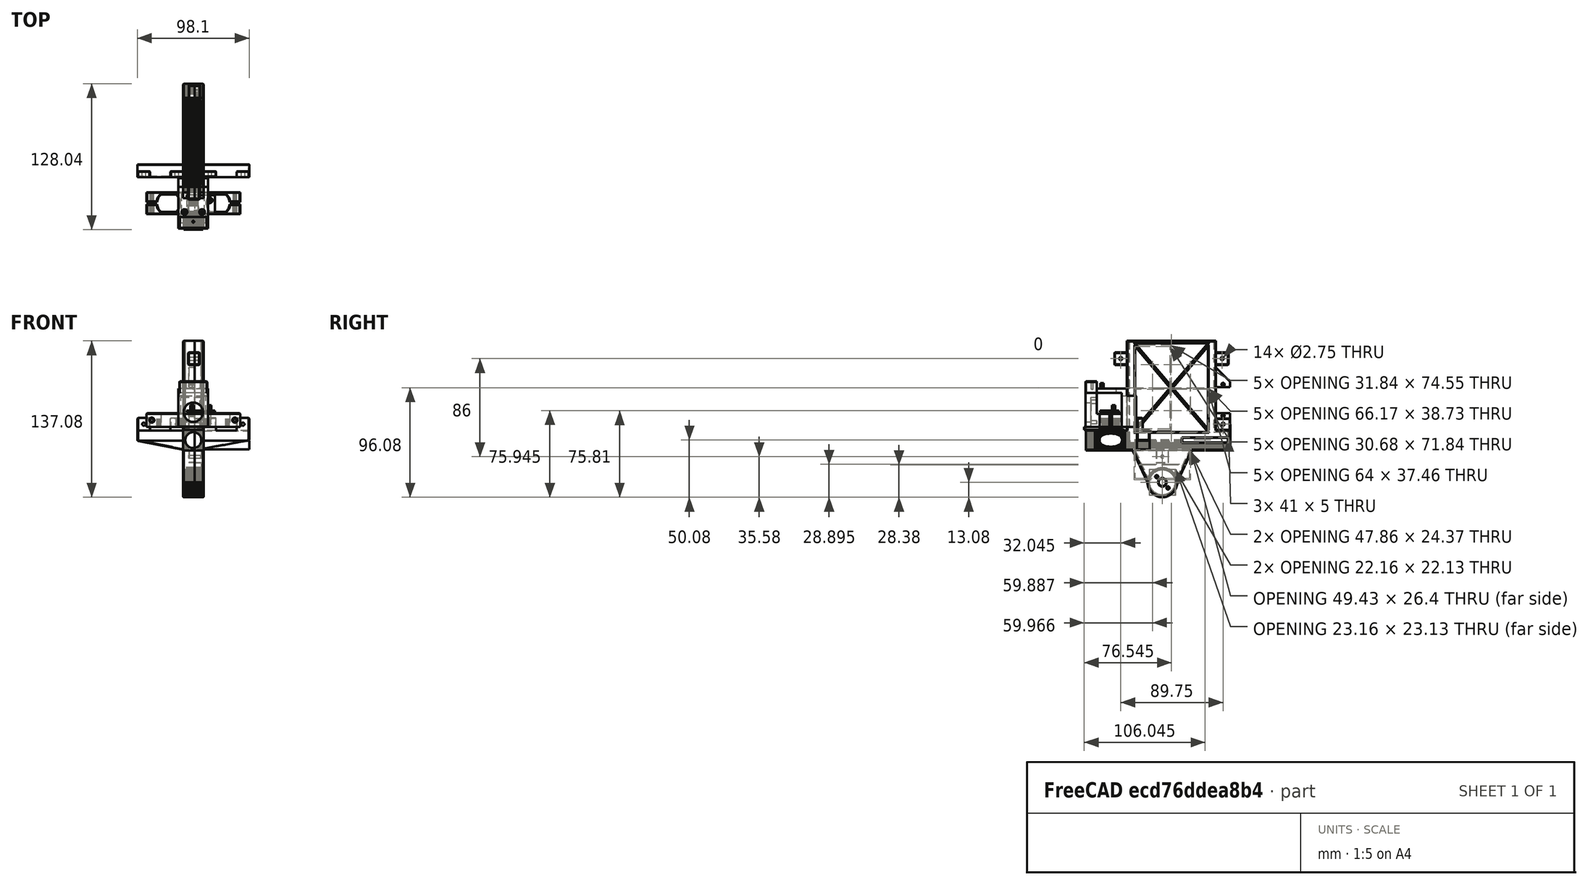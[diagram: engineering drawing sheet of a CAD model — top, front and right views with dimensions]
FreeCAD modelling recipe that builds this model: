
FCSTD DOCUMENT  (FreeCAD 1.0R39109 (Git))
Label: turret
License: All rights reserved
LicenseURL: https://en.wikipedia.org/wiki/All_rights_reserved
objects: Sketcher::SketchObject×55, Part::Extrusion×53, Part::Cut×36, Part::MultiFuse×25, Part::Feature×16, Part::Chamfer×14, Part::Box×11, Part::Fuse×8, Mesh::Feature×7, Part::Refine×4
note: 277 computed .brp shape members not serialized (recipe doc carries the construction recipe); baked Part::Feature solids carry a one-line shape summary decoded from their .brp

FEATURE [Part::Box] Box  label="querbalken"
  AttacherType = Attacher::AttachEngine3D
  Height = 30
  Length = 100
  Placement = pos=(43.7,-64,0) rot=(0,0,1;0rad)
  Width = 45
FEATURE [Part::Feature] MPU_6050_GY_521_mount002_solid  label="gyro"
  Placement = pos=(81.27,-54.1,29) rot=(0,0,1;3.14159rad)
  shape: bbox 24.5 x 16.43 x 6 mm, 2020 faces (baked)
FEATURE [Part::Box] Box001  label="basis"
  AttacherType = Attacher::AttachEngine3D
  Height = 26
  Length = 22
  Placement = pos=(38,80,2) rot=(0,0,1;0rad)
  Width = 34
FEATURE [Sketcher::SketchObject] Sketch002  label="sketch_aufnahmen"
  ArcFitTolerance = 1e-06
  AttachmentSupport = -> [Box001]
  ExternalGeometry = -> [Box001]
  FullyConstrained = true
  MakeInternals = false
  MapMode = 5
  Placement = pos=(38,80,2) rot=(1,0,0;1.5708rad)
  sketch-geometry (2):
    g0: Circle CenterX=18 CenterY=22 CenterZ=0 NormalX=0 NormalY=0 NormalZ=1 AngleXU=0 Radius=1.45
    g1: Circle CenterX=4 CenterY=4 CenterZ=0 NormalX=0 NormalY=0 NormalZ=1 AngleXU=0 Radius=1.45
  constraints (6):
    c: Diameter(g0) = 2.9
    c: Distance(g0,g-3) = 4
    c: Distance(g0,g-4) = 4
    c: Diameter(g1) = 2.9
    c: DistanceY(g-1,g1) = 4
    c: DistanceX(g-2,g1) = 4
FEATURE [Part::Extrusion] Extrude  label="extrude_aufnahmen"
  Base = -> Sketch002
  Dir = (0,-1,2e-16)
  DirMode = 2
  FaceMakerClass = Part::FaceMakerBullseye
  FaceMakerMode = 3
  LengthFwd = -5
  LengthRev = 0
  Solid = true
  Symmetric = false
FEATURE [Part::Cut] Cut
  Base = -> Box001
  Placement = pos=(0,-69,0) rot=(0,0,1;0rad)
  Refine = true
  Tool = -> Extrude
FEATURE [Sketcher::SketchObject] Sketch  label="sketch_sensor"
  ArcFitTolerance = 1e-06
  AttachmentSupport = -> [Cut]
  ExternalGeometry = -> [Cut]
  FullyConstrained = true
  MakeInternals = false
  MapMode = 5
  Placement = pos=(0,11,0) rot=(1,0,0;1.5708rad)
  sketch-geometry (1):
    g0: Circle CenterX=49 CenterY=15 CenterZ=0 NormalX=0 NormalY=0 NormalZ=1 AngleXU=0 Radius=8.5
  constraints (3):
    c: Diameter(g0) = 17
    c: Distance(g0,g-3) = 13
    c: Distance(g0,g-4) = 11
FEATURE [Part::Extrusion] Extrude001  label="extrude_sensor"
  Base = -> Sketch
  Dir = (0,-1,2e-16)
  DirMode = 2
  FaceMakerClass = Part::FaceMakerBullseye
  FaceMakerMode = 3
  LengthFwd = 20
  LengthRev = 0
  Solid = true
  Symmetric = false
FEATURE [Part::Fuse] Fusion  label="ultraschall"
  Base = -> Cut
  Placement = pos=(44.6,-2.9,0) rot=(0,0,1;0rad)
  Refine = true
  Tool = -> Extrude001
FEATURE [Part::Feature] Left_Magazine001
  shape: bbox 8 x 119 x 137.1 mm, 2276 faces, 0 solids (baked)
FEATURE [Part::Feature] Right_Magazine001
  shape: bbox 10 x 119 x 137.1 mm, 2082 faces, 0 solids (baked)
FEATURE [Part::Refine] Left_Magazine002
  Source = -> Left_Magazine001
FEATURE [Part::Refine] Right_Magazine002
  Source = -> Right_Magazine001
FEATURE [Part::Feature] Left_Magazine002_solid  label="mag_l"
  shape: bbox 8 x 119 x 137.1 mm, 1376 faces (baked)
FEATURE [Part::Feature] Right_Magazine002_solid  label="mag_r"
  shape: bbox 10 x 119 x 137.1 mm, 1299 faces (baked)
FEATURE [Part::MultiFuse] Fusion001  label="mag"
  Refine = true
  Shapes = -> [Left_Magazine002_solid,Right_Magazine002_solid]
FEATURE [Sketcher::SketchObject] Sketch004  label="muzzle_extension"
  ArcFitTolerance = 1e-06
  AttachmentSupport = -> [Fusion001]
  ExternalGeometry = -> [Fusion001]
  FullyConstrained = true
  MakeInternals = false
  MapMode = 5
  Placement = pos=(0,-53.6552,0) rot=(1,0,0;1.5708rad)
  sketch-geometry (63):
    g0: LineSegment StartX=-27.5 StartY=169.88 StartZ=0 EndX=-10.5 EndY=169.88 EndZ=0
    g1: LineSegment StartX=-10.5 StartY=169.88 StartZ=0 EndX=-10.5 EndY=151.88 EndZ=0
    g2: LineSegment StartX=-10.5 StartY=151.88 StartZ=0 EndX=-27.5 EndY=151.88 EndZ=0
    g3: LineSegment StartX=-27.5 StartY=151.88 StartZ=0 EndX=-27.5 EndY=169.88 EndZ=0
    g4: LineSegment StartX=-22.9905 StartY=166.631 StartZ=0 EndX=-22.3526 EndY=167.025 EndZ=0
    g5: LineSegment StartX=-22.3526 StartY=167.025 StartZ=0 EndX=-21.6763 EndY=167.348 EndZ=0
    g6: LineSegment StartX=-21.6763 StartY=167.348 StartZ=0 EndX=-20.9694 EndY=167.597 EndZ=0
    g7: LineSegment StartX=-20.9694 StartY=167.597 StartZ=0 EndX=-20.2398 EndY=167.77 EndZ=0
    g8: LineSegment StartX=-20.2398 StartY=167.77 StartZ=0 EndX=-19.496 EndY=167.863 EndZ=0
    g9: LineSegment StartX=-19.496 StartY=167.863 StartZ=0 EndX=-18.7466 EndY=167.876 EndZ=0
    g10: LineSegment StartX=-18.7466 StartY=167.876 StartZ=0 EndX=-18 EndY=167.808 EndZ=0
    g11: LineSegment StartX=-18 StartY=167.808 StartZ=0 EndX=-17.2744 EndY=167.664 EndZ=0
    g12: LineSegment StartX=-17.2744 StartY=167.664 StartZ=0 EndX=-16.568 EndY=167.444 EndZ=0
    g13: LineSegment StartX=-16.568 StartY=167.444 StartZ=0 EndX=-15.8889 EndY=167.151 EndZ=0
    g14: LineSegment StartX=-15.8889 StartY=167.151 StartZ=0 EndX=-15.2444 EndY=166.787 EndZ=0
    g15: LineSegment StartX=-15.2444 StartY=166.787 StartZ=0 EndX=-14.642 EndY=166.358 EndZ=0
    g16: LineSegment StartX=-14.642 StartY=166.358 StartZ=0 EndX=-14.0882 EndY=165.868 EndZ=0
    g17: LineSegment StartX=-14.0882 StartY=165.868 StartZ=0 EndX=-13.5892 EndY=165.321 EndZ=0
    g18: LineSegment StartX=-13.5892 StartY=165.321 StartZ=0 EndX=-13.1507 EndY=164.725 EndZ=0
    g19: LineSegment StartX=-13.1507 StartY=164.725 StartZ=0 EndX=-12.7776 EndY=164.087 EndZ=0
    g20: LineSegment StartX=-12.7776 StartY=164.087 StartZ=0 EndX=-12.4739 EndY=163.412 EndZ=0
    g21: LineSegment StartX=-12.4739 StartY=163.412 StartZ=0 EndX=-12.2431 EndY=162.709 EndZ=0
    g22: LineSegment StartX=-12.2431 StartY=162.709 StartZ=0 EndX=-12.0879 EndY=161.986 EndZ=0
    g23: LineSegment StartX=-12.0879 StartY=161.986 StartZ=0 EndX=-12.0098 EndY=161.25 EndZ=0
    g24: LineSegment StartX=-12.0098 StartY=161.25 StartZ=0 EndX=-12.0098 EndY=160.51 EndZ=0
    g25: LineSegment StartX=-12.0098 StartY=160.51 StartZ=0 EndX=-12.0879 EndY=159.775 EndZ=0
    g26: LineSegment StartX=-12.0879 StartY=159.775 StartZ=0 EndX=-12.2431 EndY=159.051 EndZ=0
    g27: LineSegment StartX=-12.2431 StartY=159.051 StartZ=0 EndX=-12.4739 EndY=158.348 EndZ=0
    g28: LineSegment StartX=-12.4739 StartY=158.348 StartZ=0 EndX=-12.7776 EndY=157.674 EndZ=0
    g29: LineSegment StartX=-12.7776 StartY=157.674 StartZ=0 EndX=-13.1507 EndY=157.035 EndZ=0
    g30: LineSegment StartX=-13.1507 StartY=157.035 StartZ=0 EndX=-13.5892 EndY=156.439 EndZ=0
    g31: LineSegment StartX=-13.5892 StartY=156.439 StartZ=0 EndX=-14.0882 EndY=155.893 EndZ=0
    g32: LineSegment StartX=-14.0882 StartY=155.893 StartZ=0 EndX=-14.642 EndY=155.402 EndZ=0
    g33: LineSegment StartX=-14.642 StartY=155.402 StartZ=0 EndX=-15.2444 EndY=154.973 EndZ=0
    g34: LineSegment StartX=-15.2444 StartY=154.973 StartZ=0 EndX=-15.8889 EndY=154.61 EndZ=0
    g35: LineSegment StartX=-15.8889 StartY=154.61 StartZ=0 EndX=-16.568 EndY=154.316 EndZ=0
    g36: LineSegment StartX=-16.568 StartY=154.316 StartZ=0 EndX=-17.2744 EndY=154.096 EndZ=0
    g37: LineSegment StartX=-17.2744 StartY=154.096 StartZ=0 EndX=-18 EndY=153.952 EndZ=0
    g38: LineSegment StartX=-18 StartY=153.952 StartZ=0 EndX=-18.7466 EndY=153.885 EndZ=0
    g39: LineSegment StartX=-18.7466 StartY=153.885 StartZ=0 EndX=-19.496 EndY=153.898 EndZ=0
    g40: LineSegment StartX=-19.496 StartY=153.898 StartZ=0 EndX=-20.2398 EndY=153.991 EndZ=0
    g41: LineSegment StartX=-20.2398 StartY=153.991 StartZ=0 EndX=-20.9694 EndY=154.163 EndZ=0
    g42: LineSegment StartX=-20.9694 StartY=154.163 StartZ=0 EndX=-21.6763 EndY=154.412 EndZ=0
    g43: LineSegment StartX=-21.6763 StartY=154.412 StartZ=0 EndX=-22.3526 EndY=154.735 EndZ=0
    g44: LineSegment StartX=-22.3526 StartY=154.735 StartZ=0 EndX=-22.9905 EndY=155.129 EndZ=0
    g45: LineSegment StartX=-22.9905 StartY=155.129 StartZ=0 EndX=-23.5826 EndY=155.589 EndZ=0
    g46: LineSegment StartX=-23.5826 StartY=155.589 StartZ=0 EndX=-24.1221 EndY=156.109 EndZ=0
    g47: LineSegment StartX=-24.1221 StartY=156.109 StartZ=0 EndX=-24.6029 EndY=156.684 EndZ=0
    g48: LineSegment StartX=-24.6029 StartY=156.684 StartZ=0 EndX=-25.0195 EndY=157.307 EndZ=0
    g49: LineSegment StartX=-25.0195 StartY=157.307 StartZ=0 EndX=-25.367 EndY=157.971 EndZ=0
    g50: LineSegment StartX=-25.367 StartY=157.971 StartZ=0 EndX=-25.6416 EndY=158.669 EndZ=0
    g51: LineSegment StartX=-25.6416 StartY=158.669 StartZ=0 EndX=-25.8399 EndY=159.392 EndZ=0
    g52: LineSegment StartX=-25.8399 StartY=159.392 StartZ=0 EndX=-25.9599 EndY=160.132 EndZ=0
    g53: LineSegment StartX=-25.9599 StartY=160.132 StartZ=0 EndX=-26 EndY=160.88 EndZ=0
    g54: LineSegment StartX=-26 StartY=160.88 StartZ=0 EndX=-25.9599 EndY=161.629 EndZ=0
    g55: LineSegment StartX=-25.9599 StartY=161.629 StartZ=0 EndX=-25.8399 EndY=162.369 EndZ=0
    g56: LineSegment StartX=-25.8399 StartY=162.369 StartZ=0 EndX=-25.6416 EndY=163.091 EndZ=0
    g57: LineSegment StartX=-25.6416 StartY=163.091 StartZ=0 EndX=-25.367 EndY=163.789 EndZ=0
    g58: LineSegment StartX=-25.367 StartY=163.789 StartZ=0 EndX=-25.0195 EndY=164.453 EndZ=0
    g59: LineSegment StartX=-25.0195 StartY=164.453 StartZ=0 EndX=-24.6029 EndY=165.076 EndZ=0
    g60: LineSegment StartX=-24.6029 StartY=165.076 StartZ=0 EndX=-24.1221 EndY=165.651 EndZ=0
    g61: LineSegment StartX=-24.1221 StartY=165.651 StartZ=0 EndX=-23.5826 EndY=166.172 EndZ=0
    g62: LineSegment StartX=-23.5826 StartY=166.172 StartZ=0 EndX=-22.9905 EndY=166.631 EndZ=0
  constraints (126):
    c: Coincident(g-6,g0)
    c: Coincident(g0,g-6)
    c: Coincident(g0,g1)
    c: Coincident(g1,g-5)
    c: Coincident(g1,g2)
    c: Coincident(g2,g-4)
    c: Coincident(g2,g3)
    c: Coincident(g3,g0)
    c: Coincident(g-67,g4)
    c: Coincident(g4,g-67)
    c: Coincident(g4,g5)
    c: Coincident(g5,g-8)
    c: Coincident(g5,g6)
    c: Coincident(g6,g-8)
    c: Coincident(g6,g7)
    c: Coincident(g7,g-10)
    c: Coincident(g7,g8)
    c: Coincident(g8,g-11)
    c: Coincident(g8,g9)
    c: Coincident(g9,g-12)
    c: Coincident(g9,g10)
    c: Coincident(g10,g-13)
    c: Coincident(g10,g11)
    c: Coincident(g11,g-14)
    c: Coincident(g11,g12)
    c: Coincident(g12,g-15)
    c: Coincident(g12,g13)
    c: Coincident(g13,g-16)
    c: Coincident(g13,g14)
    c: Coincident(g14,g-17)
    c: Coincident(g14,g15)
    c: Coincident(g15,g-18)
    c: Coincident(g15,g16)
    c: Coincident(g16,g-19)
    c: Coincident(g16,g17)
    c: Coincident(g17,g-20)
    c: Coincident(g17,g18)
    c: Coincident(g18,g-21)
    c: Coincident(g18,g19)
    c: Coincident(g19,g-22)
    c: Coincident(g19,g20)
    c: Coincident(g20,g-24)
    c: Coincident(g20,g21)
    c: Coincident(g21,g-25)
    c: Coincident(g21,g22)
    c: Coincident(g22,g-26)
    c: Coincident(g22,g23)
    c: Coincident(g23,g-27)
    c: Coincident(g23,g24)
    c: Coincident(g24,g-28)
    c: Coincident(g24,g25)
    c: Coincident(g25,g-29)
    c: Coincident(g25,g26)
    c: Coincident(g26,g-30)
    c: Coincident(g26,g27)
    c: Coincident(g27,g-31)
    c: Coincident(g27,g28)
    c: Coincident(g28,g-32)
    c: Coincident(g28,g29)
    c: Coincident(g29,g-33)
    c: Coincident(g29,g30)
    c: Coincident(g30,g-34)
    c: Coincident(g30,g31)
    c: Coincident(g31,g-35)
    c: Coincident(g31,g32)
    c: Coincident(g32,g-36)
    c: Coincident(g32,g33)
    c: Coincident(g33,g-37)
    c: Coincident(g33,g34)
    c: Coincident(g34,g-38)
    c: Coincident(g34,g35)
    c: Coincident(g35,g-39)
    c: Coincident(g35,g36)
    c: Coincident(g36,g-41)
    c: Coincident(g36,g37)
    c: Coincident(g37,g-42)
    c: Coincident(g37,g38)
    c: Coincident(g38,g-43)
    c: Coincident(g38,g39)
    c: Coincident(g39,g-44)
    c: Coincident(g39,g40)
    c: Coincident(g40,g-45)
    c: Coincident(g40,g41)
    c: Coincident(g41,g-46)
    c: Coincident(g41,g42)
    c: Coincident(g42,g-47)
    c: Coincident(g42,g43)
    c: Coincident(g43,g-48)
    c: Coincident(g43,g44)
    c: Coincident(g44,g-49)
    c: Coincident(g44,g45)
    c: Coincident(g45,g-50)
    c: Coincident(g45,g46)
    c: Coincident(g46,g-51)
    c: Coincident(g46,g47)
    c: Coincident(g47,g-52)
    c: Coincident(g47,g48)
    c: Coincident(g48,g-53)
    c: Coincident(g48,g49)
    c: Coincident(g49,g-54)
    c: Coincident(g49,g50)
    c: Coincident(g50,g-55)
    c: Coincident(g50,g51)
    c: Coincident(g51,g-56)
    c: Coincident(g51,g52)
    c: Coincident(g52,g-57)
    c: Coincident(g52,g53)
    c: Coincident(g53,g-58)
    c: Coincident(g53,g54)
    c: Coincident(g54,g-59)
    c: Coincident(g54,g55)
    c: Coincident(g55,g-60)
    c: Coincident(g55,g56)
    c: Coincident(g56,g-61)
    c: Coincident(g56,g57)
    c: Coincident(g57,g-62)
    c: Coincident(g57,g58)
    c: Coincident(g58,g-63)
    c: Coincident(g58,g59)
    c: Coincident(g59,g-64)
    c: Coincident(g59,g60)
    c: Coincident(g60,g-65)
    c: Coincident(g60,g61)
    c: Coincident(g61,g-66)
    c: Coincident(g61,g62)
    c: Coincident(g62,g4)
FEATURE [Sketcher::SketchObject] Sketch007
  ArcFitTolerance = 1e-06
  AttachmentSupport = -> [Box]
  ExternalGeometry = -> [Box]
  FullyConstrained = true
  MakeInternals = false
  MapMode = 5
  Placement = pos=(43.7,-64,0) rot=(1,0,0;3.14159rad)
  sketch-geometry (17):
    g0: LineSegment [constr] StartX=0 StartY=-22.5 StartZ=0 EndX=100 EndY=-22.5 EndZ=0
    g1: LineSegment [constr] StartX=50 StartY=0 StartZ=0 EndX=50 EndY=-45 EndZ=0
    g2: LineSegment [constr] StartX=27.25 StartY=0 StartZ=0 EndX=27.25 EndY=-45 EndZ=0
    g3: LineSegment [constr] StartX=71.25 StartY=-20.5 StartZ=0 EndX=71.25 EndY=-24.5 EndZ=0
    g4: LineSegment [constr] StartX=71.25 StartY=-24.5 StartZ=0 EndX=74.25 EndY=-24.5 EndZ=0
    g5: LineSegment [constr] StartX=74.25 StartY=-24.5 StartZ=0 EndX=74.25 EndY=-20.5 EndZ=0
    g6: LineSegment [constr] StartX=74.25 StartY=-20.5 StartZ=0 EndX=71.25 EndY=-20.5 EndZ=0
    g7: LineSegment [constr] StartX=25.75 StartY=-20.5 StartZ=0 EndX=25.75 EndY=-24.5 EndZ=0
    g8: LineSegment [constr] StartX=25.75 StartY=-24.5 StartZ=0 EndX=28.75 EndY=-24.5 EndZ=0
    g9: LineSegment [constr] StartX=28.75 StartY=-24.5 StartZ=0 EndX=28.75 EndY=-20.5 EndZ=0
    g10: LineSegment [constr] StartX=28.75 StartY=-20.5 StartZ=0 EndX=25.75 EndY=-20.5 EndZ=0
    g11: LineSegment [constr] StartX=72.75 StartY=0 StartZ=0 EndX=72.75 EndY=-45 EndZ=0
    g12: LineSegment [constr] StartX=32.75 StartY=0 StartZ=0 EndX=32.75 EndY=-45 EndZ=0
    g13: LineSegment StartX=40.9 StartY=0 StartZ=0 EndX=40.9 EndY=-8.25 EndZ=0
    g14: LineSegment StartX=59.1 StartY=0 StartZ=0 EndX=59.1 EndY=-8.25 EndZ=0
    g15: LineSegment StartX=40.9 StartY=-8.25 StartZ=0 EndX=59.1 EndY=-8.25 EndZ=0
    g16: LineSegment StartX=40.9 StartY=0 StartZ=0 EndX=59.1 EndY=0 EndZ=0
  constraints (54):
    c: PointOnObject(g0,g-2)
    c: Symmetric(g-3,g-3,g0)
    c: Horizontal(g0)
    c: PointOnObject(g1,g-1)
    c: Symmetric(g-4,g-4,g1)
    c: Vertical(g1)
    c: PointOnObject(g2,g-1)
    c: PointOnObject(g2,g-4)
    c: Vertical(g2)
    c: Distance(g2,g1) = 22.75
    c: Coincident(g3,g4)
    c: Coincident(g4,g5)
    c: Coincident(g5,g6)
    c: Coincident(g6,g3)
    c: Vertical(g3)
    c: Vertical(g5)
    c: Horizontal(g4)
    c: Horizontal(g6)
    c: Distance(g5,g3) = 3
    c: Distance(g3,g4) = 5
    c: Coincident(g7,g8)
    c: Coincident(g8,g9)
    c: Coincident(g9,g10)
    c: Coincident(g10,g7)
    c: Vertical(g7)
    c: Vertical(g9)
    c: Horizontal(g8)
    c: Horizontal(g10)
    c: Distance(g9,g7) = 3
    c: Distance(g7,g8) = 5
    c: PointOnObject(g11,g-1)
    c: PointOnObject(g11,g-4)
    c: Vertical(g11)
    c: Distance(g11,g1) = 22.75
    c: Distance(g3,g11) = 1.5
    c: Distance(g4,g0) = 2
    c: Distance(g7,g2) = 1.5
    c: Distance(g8,g0) = 2
    c: PointOnObject(g12,g-1)
    c: PointOnObject(g12,g-4)
    c: Vertical(g12)
    c: Distance(g2,g12) = 5.5
    c: PointOnObject(g13,g-1)
    c: Vertical(g13)
    c: Distance(g13,g1) = 9.1
    c: PointOnObject(g14,g-1)
    c: Vertical(g14)
    c: Distance(g14,g1) = 9.1
    c: Coincident(g15,g13)
    c: Coincident(g15,g14)
    c: Horizontal(g15)
    c: Distance(g13,g0) = 14.25
    c: Coincident(g16,g13)
    c: Coincident(g16,g14)
FEATURE [Part::Feature] Fusion006  label="servo_cut_with_screw_r"
  shape: bbox 31 x 41.99 x 29 mm, 460 faces (baked)
FEATURE [Sketcher::SketchObject] Sketch011
  ArcFitTolerance = 1e-06
  AttachmentSupport = -> [Fusion006]
  ExternalGeometry = -> [Fusion006]
  FullyConstrained = true
  MakeInternals = false
  MapMode = 5
  Placement = pos=(45.95,0,0) rot=(0.57735,-0.57735,-0.57735;2.0944rad)
  sketch-geometry (4):
    g0: LineSegment StartX=34 StartY=3.5 StartZ=0 EndX=49 EndY=3.5 EndZ=0
    g1: LineSegment StartX=34 StartY=13.5 StartZ=0 EndX=49 EndY=13.5 EndZ=0
    g2: LineSegment StartX=34 StartY=13.5 StartZ=0 EndX=34 EndY=3.5 EndZ=0
    g3: LineSegment StartX=49 StartY=13.5 StartZ=0 EndX=49 EndY=3.5 EndZ=0
  constraints (12):
    c: PointOnObject(g0,g-3)
    c: PointOnObject(g0,g-4)
    c: Horizontal(g0)
    c: Distance(g0,g-3) = 3.5
    c: PointOnObject(g1,g-3)
    c: PointOnObject(g1,g-4)
    c: Horizontal(g1)
    c: DistanceY(g0,g1) = 10
    c: Coincident(g2,g1)
    c: Coincident(g2,g0)
    c: Coincident(g3,g1)
    c: Coincident(g3,g0)
FEATURE [Part::Extrusion] Extrude007
  Base = -> Sketch011
  Dir = (-1,0,0)
  DirMode = 2
  FaceMakerClass = Part::FaceMakerBullseye
  FaceMakerMode = 3
  LengthFwd = 10
  LengthRev = 0
  Solid = true
  Symmetric = false
FEATURE [Part::MultiFuse] Fusion007  label="servu_cut_with_screw_and_cabel_r"
  Refine = true
  Shapes = -> [Fusion006,Extrude007]
FEATURE [Sketcher::SketchObject] Sketch012
  ArcFitTolerance = 1e-06
  AttachmentSupport = -> [Fusion007]
  ExternalGeometry = -> [Fusion007]
  FullyConstrained = true
  MakeInternals = false
  MapMode = 5
  Placement = pos=(0,0,21.5) rot=(0,0,1;0rad)
  sketch-geometry (18):
    g0: LineSegment StartX=51.13 StartY=-34 StartZ=0 EndX=51.5875 EndY=-33.3211 EndZ=0
    g1: LineSegment StartX=51.5875 StartY=-33.3211 StartZ=0 EndX=52.0856 EndY=-32.6702 EndZ=0
    g2: LineSegment StartX=52.0856 StartY=-32.6702 StartZ=0 EndX=52.6209 EndY=-32.0496 EndZ=0
    g3: LineSegment StartX=52.6209 StartY=-32.0496 StartZ=0 EndX=53.1917 EndY=-31.4614 EndZ=0
    g4: LineSegment StartX=53.1917 StartY=-31.4614 StartZ=0 EndX=53.7958 EndY=-30.9075 EndZ=0
    g5: LineSegment StartX=53.7958 StartY=-30.9075 StartZ=0 EndX=54.4313 EndY=-30.39 EndZ=0
    g6: LineSegment StartX=54.4313 StartY=-30.39 StartZ=0 EndX=55.0961 EndY=-29.9106 EndZ=0
    g7: LineSegment StartX=55.0961 StartY=-29.9106 StartZ=0 EndX=45.95 EndY=-34 EndZ=0
    g8: LineSegment StartX=45.95 StartY=-34 StartZ=0 EndX=51.13 EndY=-34 EndZ=0
    g9: LineSegment StartX=45.95 StartY=-49 StartZ=0 EndX=51.1284 EndY=-49 EndZ=0
    g10: LineSegment StartX=51.1284 StartY=-49 StartZ=0 EndX=51.5875 EndY=-49.679 EndZ=0
    g11: LineSegment StartX=51.5875 StartY=-49.679 StartZ=0 EndX=52.0856 EndY=-50.3298 EndZ=0
    g12: LineSegment StartX=52.0856 StartY=-50.3298 StartZ=0 EndX=52.6209 EndY=-50.9505 EndZ=0
    g13: LineSegment StartX=52.6209 StartY=-50.9505 StartZ=0 EndX=53.1917 EndY=-51.5387 EndZ=0
    g14: LineSegment StartX=53.1917 StartY=-51.5387 StartZ=0 EndX=53.7958 EndY=-52.0925 EndZ=0
    g15: LineSegment StartX=53.7958 StartY=-52.0925 StartZ=0 EndX=54.4313 EndY=-52.6101 EndZ=0
    g16: LineSegment StartX=54.4313 StartY=-52.6101 StartZ=0 EndX=55.0961 EndY=-53.0895 EndZ=0
    g17: LineSegment StartX=55.0961 StartY=-53.0895 StartZ=0 EndX=45.95 EndY=-49 EndZ=0
  constraints (37):
    c: Coincident(g0,g-5)
    c: Coincident(g0,g1)
    c: Coincident(g1,g-6)
    c: Coincident(g1,g2)
    c: Coincident(g2,g-7)
    c: Coincident(g2,g3)
    c: Coincident(g3,g-8)
    c: Coincident(g3,g4)
    c: Coincident(g4,g-9)
    c: Coincident(g4,g5)
    c: Coincident(g5,g-10)
    c: Coincident(g6,g5)
    c: Coincident(g6,g-10)
    c: Coincident(g7,g6)
    c: Coincident(g7,g-19)
    c: Coincident(g8,g7)
    c: Coincident(g8,g0)
    c: Horizontal(g8)
    c: Coincident(g-19,g9)
    c: Coincident(g9,g-12)
    c: Coincident(g9,g10)
    c: Coincident(g10,g-13)
    c: Coincident(g10,g11)
    c: Coincident(g11,g-14)
    c: Coincident(g11,g12)
    c: Coincident(g12,g-15)
    c: Coincident(g12,g13)
    c: Coincident(g13,g-16)
    c: Coincident(g13,g14)
    c: Coincident(g14,g-17)
    c: Coincident(g14,g15)
    c: Coincident(g15,g-18)
    c: Coincident(g15,g16)
    c: Coincident(g16,g-18)
    c: Coincident(g16,g17)
    c: Coincident(g17,g9)
    c: Distance(g7,g0) = 5.18
FEATURE [Part::Extrusion] Extrude008
  Base = -> Sketch012
  Dir = (0,0,1)
  DirMode = 2
  FaceMakerClass = Part::FaceMakerBullseye
  FaceMakerMode = 3
  LengthFwd = -21.5
  LengthRev = 0
  Solid = true
  Symmetric = false
FEATURE [Part::Fuse] Fusion010  label="servo_cut_with_screw_and_cabel_and_cabelpuffer_r"
  Base = -> Fusion007
  Refine = true
  Tool = -> Extrude008
FEATURE [Part::Feature] Fusion011  label="servo_cut_with_screw_and_cabel_and_cabelpuffer_l"
  Placement = pos=(187.4,-83,0) rot=(0,0,1;3.14159rad)
  shape: bbox 41 x 41.99 x 29 mm, 476 faces (baked)
FEATURE [Part::Cut] Cut003
  Base = -> Box
  Refine = true
  Tool = -> Fusion010
FEATURE [Part::Extrusion] Extrude009
  Base = -> Sketch007
  Dir = (0,0,-1)
  DirMode = 2
  FaceMakerClass = Part::FaceMakerBullseye
  FaceMakerMode = 3
  LengthFwd = -30
  LengthRev = 0
  Placement = pos=(0,36.75,0) rot=(0,0,1;0rad)
  Solid = true
  Symmetric = false
FEATURE [Part::Cut] Cut004
  Base = -> Cut003
  Refine = true
  Tool = -> Fusion011
FEATURE [Part::Cut] Cut005
  Base = -> Cut004
  Refine = true
  Tool = -> Extrude009
FEATURE [Sketcher::SketchObject] Sketch013
  ArcFitTolerance = 1e-06
  AttachmentSupport = -> [Cut005]
  ExternalGeometry = -> [Cut005]
  FullyConstrained = true
  MakeInternals = false
  MapMode = 5
  Placement = pos=(0,0,30) rot=(0,0,1;0rad)
  sketch-geometry (4):
    g0: LineSegment StartX=81.45 StartY=-64 StartZ=0 EndX=81.45 EndY=-54 EndZ=0
    g1: LineSegment StartX=105.95 StartY=-64 StartZ=0 EndX=105.95 EndY=-54 EndZ=0
    g2: LineSegment StartX=81.45 StartY=-54 StartZ=0 EndX=105.95 EndY=-54 EndZ=0
    g3: LineSegment StartX=81.45 StartY=-64 StartZ=0 EndX=105.95 EndY=-64 EndZ=0
  constraints (12):
    c: PointOnObject(g0,g-9)
    c: Vertical(g0)
    c: PointOnObject(g1,g-9)
    c: Vertical(g1)
    c: Coincident(g2,g0)
    c: Coincident(g2,g1)
    c: Horizontal(g2)
    c: Distance(g0,g0) = 10
    c: Distance(g0,g1) = 24.5
    c: Distance(g-9,g1) = 37.75
    c: Coincident(g3,g0)
    c: Coincident(g3,g1)
FEATURE [Sketcher::SketchObject] Sketch016
  ArcFitTolerance = 1e-06
  AttachmentSupport = -> [Fusion]
  ExternalGeometry = -> [Fusion]
  FullyConstrained = true
  MakeInternals = false
  MapMode = 5
  Placement = pos=(44.6,42.1,0) rot=(0,0.707107,0.707107;3.14159rad)
  sketch-geometry (4):
    g0: LineSegment StartX=-60 StartY=28 StartZ=0 EndX=-60 EndY=2 EndZ=0
    g1: LineSegment StartX=-60 StartY=2 StartZ=0 EndX=-38 EndY=2 EndZ=0
    g2: LineSegment StartX=-38 StartY=2 StartZ=0 EndX=-38 EndY=28 EndZ=0
    g3: LineSegment StartX=-38 StartY=28 StartZ=0 EndX=-60 EndY=28 EndZ=0
  constraints (8):
    c: Coincident(g0,g-4)
    c: Coincident(g0,g-6)
    c: Coincident(g0,g1)
    c: Coincident(g1,g-6)
    c: Coincident(g1,g2)
    c: Coincident(g2,g-5)
    c: Coincident(g2,g3)
    c: Coincident(g3,g0)
FEATURE [Part::Extrusion] Extrude010
  Base = -> Sketch016
  Dir = (0,1,-2e-16)
  DirMode = 2
  FaceMakerClass = Part::FaceMakerBullseye
  FaceMakerMode = 3
  LengthFwd = -7.25
  LengthRev = 0
  Solid = true
  Symmetric = false
FEATURE [Part::MultiFuse] Fusion012
  Refine = true
  Shapes = -> [Cut005,MPU_6050_GY_521_mount002_solid]
FEATURE [Part::Extrusion] Extrude011
  Base = -> Sketch013
  Dir = (0,0,1)
  DirMode = 2
  FaceMakerClass = Part::FaceMakerBullseye
  FaceMakerMode = 3
  LengthFwd = 10
  LengthRev = 0
  Solid = true
  Symmetric = false
FEATURE [Part::MultiFuse] Fusion013
  Refine = true
  Shapes = -> [Fusion012,Extrude011]
FEATURE [Part::Cut] Cut006
  Base = -> Fusion
  Placement = pos=(0.1,-67.1,-2) rot=(0,0,1;0rad)
  Refine = true
  Tool = -> Extrude010
FEATURE [Part::Cut] Cut007
  Base = -> Fusion013
  Refine = true
  Tool = -> Cut006
FEATURE [Sketcher::SketchObject] Sketch017
  ArcFitTolerance = 1e-06
  AttachmentSupport = -> [Cut007]
  ExternalGeometry = -> [Cut007]
  FullyConstrained = true
  MakeInternals = false
  MapMode = 5
  Placement = pos=(0,0,30) rot=(0,0,1;0rad)
  sketch-geometry (5):
    g0: LineSegment [constr] StartX=43.7 StartY=-32.25 StartZ=0 EndX=143.7 EndY=-32.25 EndZ=0
    g1: LineSegment StartX=85.2001 StartY=-37.25 StartZ=0 EndX=85.2001 EndY=-32.25 EndZ=0
    g2: LineSegment StartX=102.2 StartY=-37.25 StartZ=0 EndX=102.2 EndY=-32.2139 EndZ=0
    g3: LineSegment StartX=85.2001 StartY=-37.25 StartZ=0 EndX=102.2 EndY=-37.25 EndZ=0
    g4: LineSegment StartX=85.2001 StartY=-32.25 StartZ=0 EndX=102.2 EndY=-32.2139 EndZ=0
  constraints (16):
    c: PointOnObject(g0,g-14)
    c: PointOnObject(g0,g-8)
    c: Horizontal(g0)
    c: Distance(g0,g-14) = 13.25
    c: Distance(g1) = 5
    c: Vertical(g1)
    c: PointOnObject(g1,g0)
    c: Distance(g2,g-6) = 5
    c: Distance(g2,g0) = 41.5
    c: Distance(g2,g1) = 17
    c: Coincident(g3,g1)
    c: Coincident(g3,g2)
    c: Horizontal(g3)
    c: Distance(g2,g1) = 17
    c: Coincident(g4,g1)
    c: Coincident(g4,g2)
FEATURE [Part::Extrusion] Extrude012
  Base = -> Sketch017
  Dir = (0,0,1)
  DirMode = 2
  FaceMakerClass = Part::FaceMakerBullseye
  FaceMakerMode = 3
  LengthFwd = -15
  LengthRev = 0
  Solid = true
  Symmetric = false
FEATURE [Part::Cut] Cut008  label="arm_final"
  Base = -> Cut007
  Placement = pos=(-112.75,2,170) rot=(0,0,1;0rad)
  Refine = true
  Tool = -> Extrude012
FEATURE [Part::Chamfer] Chamfer  label="arm-final-smoothed-edges"
  Base = -> Cut008
  EdgeLinks = -> Cut008 [Edge1,Edge4,Edge5,Edge6,Edge7,Edge8,Edge9,Edge10,Edge11,Edge16,Edge17,Edge21,Edge23,Edge130,Edge131,Edge132,Edge137,Edge140,Edge142,Edge387]
  Edges = 20 edges r=0.5: [Edge1,Edge4,Edge5,Edge6,Edge7,Edge8,Edge9,Edge10,Edge11,Edge16,Edge17,Edge21,Edge23,Edge130,Edge131,Edge132,Edge137,Edge140,Edge142,Edge387]
FEATURE [Sketcher::SketchObject] Sketch018  label="Left-Mag-Nozzle-Enlargement-Sketch"
  ArcFitTolerance = 1e-06
  AttachmentSupport = -> [Left_Magazine002]
  ExternalGeometry = -> [Left_Magazine002]
  FullyConstrained = true
  MakeInternals = false
  MapMode = 5
  Placement = pos=(0,-53.6552,0) rot=(1,0,0;1.5708rad)
  sketch-geometry (34):
    g0: LineSegment StartX=-18 StartY=169.88 StartZ=0 EndX=-10.5 EndY=169.88 EndZ=0
    g1: LineSegment StartX=-10.5 StartY=169.88 StartZ=0 EndX=-10 EndY=169.38 EndZ=0
    g2: LineSegment StartX=-10 StartY=169.38 StartZ=0 EndX=-10 EndY=152.38 EndZ=0
    g3: LineSegment StartX=-10 StartY=152.38 StartZ=0 EndX=-10.5 EndY=151.88 EndZ=0
    g4: LineSegment StartX=-10.5 StartY=151.88 StartZ=0 EndX=-18 EndY=151.88 EndZ=0
    g5: LineSegment StartX=-18 StartY=151.88 StartZ=0 EndX=-18 EndY=153.952 EndZ=0
    g6: LineSegment StartX=-18 StartY=153.952 StartZ=0 EndX=-17.2744 EndY=154.096 EndZ=0
    g7: LineSegment StartX=-17.2744 StartY=154.096 StartZ=0 EndX=-16.568 EndY=154.316 EndZ=0
    g8: LineSegment StartX=-16.568 StartY=154.316 StartZ=0 EndX=-15.8889 EndY=154.61 EndZ=0
    g9: LineSegment StartX=-15.8889 StartY=154.61 StartZ=0 EndX=-15.2444 EndY=154.973 EndZ=0
    g10: LineSegment StartX=-15.2444 StartY=154.973 StartZ=0 EndX=-14.642 EndY=155.402 EndZ=0
    g11: LineSegment StartX=-14.642 StartY=155.402 StartZ=0 EndX=-14.0882 EndY=155.893 EndZ=0
    g12: LineSegment StartX=-14.0882 StartY=155.893 StartZ=0 EndX=-13.5892 EndY=156.439 EndZ=0
    g13: LineSegment StartX=-13.5892 StartY=156.439 StartZ=0 EndX=-13.1507 EndY=157.035 EndZ=0
    g14: LineSegment StartX=-13.1507 StartY=157.035 StartZ=0 EndX=-12.7776 EndY=157.674 EndZ=0
    g15: LineSegment StartX=-12.7776 StartY=157.674 StartZ=0 EndX=-12.4739 EndY=158.348 EndZ=0
    g16: LineSegment StartX=-12.4739 StartY=158.348 StartZ=0 EndX=-12.2431 EndY=159.051 EndZ=0
    g17: LineSegment StartX=-12.2431 StartY=159.051 StartZ=0 EndX=-12.0879 EndY=159.775 EndZ=0
    g18: LineSegment StartX=-12.0879 StartY=159.775 StartZ=0 EndX=-12.0098 EndY=160.51 EndZ=0
    g19: LineSegment StartX=-12.0098 StartY=160.51 StartZ=0 EndX=-12.0098 EndY=161.25 EndZ=0
    g20: LineSegment StartX=-12.0098 StartY=161.25 StartZ=0 EndX=-12.0879 EndY=161.986 EndZ=0
    g21: LineSegment StartX=-12.0879 StartY=161.986 StartZ=0 EndX=-12.2431 EndY=162.709 EndZ=0
    g22: LineSegment StartX=-12.2431 StartY=162.709 StartZ=0 EndX=-12.4739 EndY=163.412 EndZ=0
    g23: LineSegment StartX=-12.4739 StartY=163.412 StartZ=0 EndX=-12.7776 EndY=164.087 EndZ=0
    g24: LineSegment StartX=-12.7776 StartY=164.087 StartZ=0 EndX=-13.1507 EndY=164.725 EndZ=0
    g25: LineSegment StartX=-13.1507 StartY=164.725 StartZ=0 EndX=-13.5892 EndY=165.321 EndZ=0
    g26: LineSegment StartX=-13.5892 StartY=165.321 StartZ=0 EndX=-14.0882 EndY=165.868 EndZ=0
    g27: LineSegment StartX=-14.0882 StartY=165.868 StartZ=0 EndX=-14.642 EndY=166.358 EndZ=0
    g28: LineSegment StartX=-14.642 StartY=166.358 StartZ=0 EndX=-15.2444 EndY=166.787 EndZ=0
    g29: LineSegment StartX=-15.2444 StartY=166.787 StartZ=0 EndX=-15.8889 EndY=167.151 EndZ=0
    g30: LineSegment StartX=-15.8889 StartY=167.151 StartZ=0 EndX=-16.568 EndY=167.444 EndZ=0
    g31: LineSegment StartX=-16.568 StartY=167.444 StartZ=0 EndX=-17.2744 EndY=167.664 EndZ=0
    g32: LineSegment StartX=-17.2744 StartY=167.664 StartZ=0 EndX=-18 EndY=167.808 EndZ=0
    g33: LineSegment StartX=-18 StartY=167.808 StartZ=0 EndX=-18 EndY=169.88 EndZ=0
  constraints (68):
    c: Coincident(g-9,g0)
    c: Coincident(g0,g-4)
    c: Coincident(g0,g1)
    c: Coincident(g1,g-5)
    c: Coincident(g1,g2)
    c: Coincident(g2,g-6)
    c: Coincident(g2,g3)
    c: Coincident(g3,g-7)
    c: Coincident(g3,g4)
    c: Coincident(g4,g-8)
    c: Coincident(g4,g5)
    c: Coincident(g5,g-36)
    c: Coincident(g5,g6)
    c: Coincident(g6,g-36)
    c: Coincident(g6,g7)
    c: Coincident(g7,g-35)
    c: Coincident(g7,g8)
    c: Coincident(g8,g-34)
    c: Coincident(g8,g9)
    c: Coincident(g9,g-33)
    c: Coincident(g9,g10)
    c: Coincident(g10,g-32)
    c: Coincident(g10,g11)
    c: Coincident(g11,g-31)
    c: Coincident(g11,g12)
    c: Coincident(g12,g-30)
    c: Coincident(g12,g13)
    c: Coincident(g13,g-29)
    c: Coincident(g13,g14)
    c: Coincident(g14,g-28)
    c: Coincident(g14,g15)
    c: Coincident(g15,g-27)
    c: Coincident(g15,g16)
    c: Coincident(g16,g-26)
    c: Coincident(g16,g17)
    c: Coincident(g17,g-25)
    c: Coincident(g17,g18)
    c: Coincident(g18,g-24)
    c: Coincident(g18,g19)
    c: Coincident(g19,g-23)
    c: Coincident(g19,g20)
    c: Coincident(g20,g-22)
    c: Coincident(g20,g21)
    c: Coincident(g21,g-21)
    c: Coincident(g21,g22)
    c: Coincident(g22,g-20)
    c: Coincident(g22,g23)
    c: Coincident(g23,g-19)
    c: Coincident(g23,g24)
    c: Coincident(g24,g-18)
    c: Coincident(g24,g25)
    c: Coincident(g25,g-17)
    c: Coincident(g25,g26)
    c: Coincident(g26,g-16)
    c: Coincident(g26,g27)
    c: Coincident(g27,g-15)
    c: Coincident(g27,g28)
    c: Coincident(g28,g-14)
    c: Coincident(g28,g29)
    c: Coincident(g29,g-13)
    c: Coincident(g29,g30)
    c: Coincident(g30,g-12)
    c: Coincident(g30,g31)
    c: Coincident(g31,g-11)
    c: Coincident(g31,g32)
    c: Coincident(g32,g-10)
    c: Coincident(g32,g33)
    c: Coincident(g33,g0)
FEATURE [Part::Extrusion] Extrude014  label="Left-Mag-Nozzle-Enlargement"
  Base = -> Sketch018
  Dir = (0,-1,2e-16)
  DirMode = 2
  FaceMakerClass = Part::FaceMakerBullseye
  FaceMakerMode = 3
  LengthFwd = 7.45
  LengthRev = 1
  Solid = true
  Symmetric = false
FEATURE [Part::Feature] Left_Magazine002_solid001  label="Left_Magazine002 (Solid)"
  shape: bbox 8 x 119 x 137.1 mm, 1376 faces (baked)
FEATURE [Part::Fuse] Fusion014  label="Left-Mag-Enlarged"
  Base = -> Extrude014
  Tool = -> Left_Magazine002_solid001
FEATURE [Part::Feature] Right_Magazine002_solid001  label="Right_Magazine002 (Solid)"
  shape: bbox 10 x 119 x 137.1 mm, 1299 faces (baked)
FEATURE [Sketcher::SketchObject] Sketch019  label="Right-Mag-Nozzle-Enlargement-Sketch"
  ArcFitTolerance = 1e-06
  AttachmentSupport = -> [Right_Magazine002_solid001]
  ExternalGeometry = -> [Right_Magazine002_solid001]
  FullyConstrained = true
  MakeInternals = false
  MapMode = 5
  Placement = pos=(0,-53.6552,0) rot=(1,0,0;1.5708rad)
  sketch-geometry (39):
    g0: LineSegment StartX=-27.5 StartY=169.88 StartZ=0 EndX=-28 EndY=169.38 EndZ=0
    g1: LineSegment StartX=-28 StartY=169.38 StartZ=0 EndX=-28 EndY=152.38 EndZ=0
    g2: LineSegment StartX=-28 StartY=152.38 StartZ=0 EndX=-27.5 EndY=151.88 EndZ=0
    g3: LineSegment StartX=-27.5 StartY=151.88 StartZ=0 EndX=-18 EndY=151.88 EndZ=0
    g4: LineSegment StartX=-18 StartY=151.88 StartZ=0 EndX=-18 EndY=153.952 EndZ=0
    g5: LineSegment StartX=-18 StartY=153.952 StartZ=0 EndX=-18.7466 EndY=153.885 EndZ=0
    g6: LineSegment StartX=-18.7466 StartY=153.885 StartZ=0 EndX=-19.496 EndY=153.898 EndZ=0
    g7: LineSegment StartX=-19.496 StartY=153.898 StartZ=0 EndX=-20.2398 EndY=153.991 EndZ=0
    g8: LineSegment StartX=-20.2398 StartY=153.991 StartZ=0 EndX=-20.9694 EndY=154.163 EndZ=0
    g9: LineSegment StartX=-20.9694 StartY=154.163 StartZ=0 EndX=-21.6763 EndY=154.412 EndZ=0
    g10: LineSegment StartX=-21.6763 StartY=154.412 StartZ=0 EndX=-22.3526 EndY=154.735 EndZ=0
    g11: LineSegment StartX=-22.3526 StartY=154.735 StartZ=0 EndX=-22.9905 EndY=155.129 EndZ=0
    g12: LineSegment StartX=-22.9905 StartY=155.129 StartZ=0 EndX=-23.5826 EndY=155.589 EndZ=0
    g13: LineSegment StartX=-23.5826 StartY=155.589 StartZ=0 EndX=-24.1221 EndY=156.109 EndZ=0
    g14: LineSegment StartX=-24.1221 StartY=156.109 StartZ=0 EndX=-24.6029 EndY=156.684 EndZ=0
    g15: LineSegment StartX=-24.6029 StartY=156.684 StartZ=0 EndX=-25.0195 EndY=157.307 EndZ=0
    g16: LineSegment StartX=-25.0195 StartY=157.307 StartZ=0 EndX=-25.367 EndY=157.971 EndZ=0
    g17: LineSegment StartX=-25.367 StartY=157.971 StartZ=0 EndX=-25.6416 EndY=158.669 EndZ=0
    g18: LineSegment StartX=-25.6416 StartY=158.669 StartZ=0 EndX=-25.8399 EndY=159.392 EndZ=0
    g19: LineSegment StartX=-25.8399 StartY=159.392 StartZ=0 EndX=-25.9599 EndY=160.132 EndZ=0
    g20: LineSegment StartX=-25.9599 StartY=160.132 StartZ=0 EndX=-26 EndY=160.88 EndZ=0
    g21: LineSegment StartX=-26 StartY=160.88 StartZ=0 EndX=-25.9599 EndY=161.629 EndZ=0
    g22: LineSegment StartX=-25.9599 StartY=161.629 StartZ=0 EndX=-25.8399 EndY=162.369 EndZ=0
    g23: LineSegment StartX=-25.8399 StartY=162.369 StartZ=0 EndX=-25.6416 EndY=163.091 EndZ=0
    g24: LineSegment StartX=-25.6416 StartY=163.091 StartZ=0 EndX=-25.367 EndY=163.789 EndZ=0
    g25: LineSegment StartX=-25.367 StartY=163.789 StartZ=0 EndX=-25.0195 EndY=164.453 EndZ=0
    g26: LineSegment StartX=-25.0195 StartY=164.453 StartZ=0 EndX=-24.6029 EndY=165.076 EndZ=0
    g27: LineSegment StartX=-24.6029 StartY=165.076 StartZ=0 EndX=-24.1221 EndY=165.651 EndZ=0
    g28: LineSegment StartX=-24.1221 StartY=165.651 StartZ=0 EndX=-23.5826 EndY=166.172 EndZ=0
    g29: LineSegment StartX=-23.5826 StartY=166.172 StartZ=0 EndX=-22.9905 EndY=166.631 EndZ=0
    g30: LineSegment StartX=-22.9905 StartY=166.631 StartZ=0 EndX=-22.3526 EndY=167.025 EndZ=0
    g31: LineSegment StartX=-22.3526 StartY=167.025 StartZ=0 EndX=-21.6763 EndY=167.348 EndZ=0
    g32: LineSegment StartX=-21.6763 StartY=167.348 StartZ=0 EndX=-20.9694 EndY=167.597 EndZ=0
    g33: LineSegment StartX=-20.9694 StartY=167.597 StartZ=0 EndX=-20.2398 EndY=167.77 EndZ=0
    g34: LineSegment StartX=-20.2398 StartY=167.77 StartZ=0 EndX=-19.496 EndY=167.863 EndZ=0
    g35: LineSegment StartX=-19.496 StartY=167.863 StartZ=0 EndX=-18.7466 EndY=167.876 EndZ=0
    g36: LineSegment StartX=-18.7466 StartY=167.876 StartZ=0 EndX=-18 EndY=167.808 EndZ=0
    g37: LineSegment StartX=-18 StartY=167.808 StartZ=0 EndX=-18 EndY=169.88 EndZ=0
    g38: LineSegment StartX=-18 StartY=169.88 StartZ=0 EndX=-27.5 EndY=169.88 EndZ=0
  constraints (78):
    c: Coincident(g-9,g0)
    c: Coincident(g0,g-9)
    c: Coincident(g0,g1)
    c: Coincident(g1,g-8)
    c: Coincident(g1,g2)
    c: Coincident(g2,g-7)
    c: Coincident(g2,g3)
    c: Coincident(g3,g-6)
    c: Coincident(g3,g4)
    c: Coincident(g4,g-41)
    c: Coincident(g4,g5)
    c: Coincident(g5,g-41)
    c: Coincident(g5,g6)
    c: Coincident(g6,g-40)
    c: Coincident(g6,g7)
    c: Coincident(g7,g-39)
    c: Coincident(g7,g8)
    c: Coincident(g8,g-38)
    c: Coincident(g8,g9)
    c: Coincident(g9,g-37)
    c: Coincident(g9,g10)
    c: Coincident(g10,g-26)
    c: Coincident(g10,g11)
    c: Coincident(g11,g-27)
    c: Coincident(g11,g12)
    c: Coincident(g12,g-28)
    c: Coincident(g12,g13)
    c: Coincident(g13,g-29)
    c: Coincident(g13,g14)
    c: Coincident(g14,g-30)
    c: Coincident(g14,g15)
    c: Coincident(g15,g-31)
    c: Coincident(g15,g16)
    c: Coincident(g16,g-32)
    c: Coincident(g16,g17)
    c: Coincident(g17,g-33)
    c: Coincident(g17,g18)
    c: Coincident(g18,g-34)
    c: Coincident(g18,g19)
    c: Coincident(g19,g-35)
    c: Coincident(g19,g20)
    c: Coincident(g20,g-36)
    c: Coincident(g20,g21)
    c: Coincident(g21,g-36)
    c: Coincident(g21,g22)
    c: Coincident(g22,g-24)
    c: Coincident(g22,g23)
    c: Coincident(g23,g-23)
    c: Coincident(g23,g24)
    c: Coincident(g24,g-22)
    c: Coincident(g24,g25)
    c: Coincident(g25,g-21)
    c: Coincident(g25,g26)
    c: Coincident(g26,g-20)
    c: Coincident(g26,g27)
    c: Coincident(g27,g-19)
    c: Coincident(g27,g28)
    c: Coincident(g28,g-18)
    c: Coincident(g28,g29)
    c: Coincident(g29,g-17)
    c: Coincident(g29,g30)
    c: Coincident(g30,g-16)
    c: Coincident(g30,g31)
    c: Coincident(g31,g-15)
    c: Coincident(g31,g32)
    c: Coincident(g32,g-14)
    c: Coincident(g32,g33)
    c: Coincident(g33,g-13)
    c: Coincident(g33,g34)
    c: Coincident(g34,g-12)
    c: Coincident(g34,g35)
    c: Coincident(g35,g-11)
    c: Coincident(g35,g36)
    c: Coincident(g36,g-10)
    c: Coincident(g36,g37)
    c: Coincident(g37,g-4)
    c: Coincident(g37,g38)
    c: Coincident(g38,g0)
FEATURE [Part::Extrusion] Extrude015  label="Right-Mag-Nozzle-Enlargement"
  Base = -> Sketch019
  Dir = (0,-1,2e-16)
  DirMode = 2
  FaceMakerClass = Part::FaceMakerBullseye
  FaceMakerMode = 3
  LengthFwd = 7.45
  LengthRev = 1
  Solid = true
  Symmetric = false
FEATURE [Part::Fuse] Fusion015  label="Right-Mag-Enlarged"
  Base = -> Right_Magazine002_solid001
  Tool = -> Extrude015
FEATURE [Sketcher::SketchObject] Sketch021  label="Left-Mag-Arm-Screwin-Sketch"
  ArcFitTolerance = 1e-06
  AttachmentSupport = -> [Fusion014]
  ExternalGeometry = -> [Chamfer,Fusion014]
  FullyConstrained = true
  MakeInternals = false
  MapMode = 5
  Placement = pos=(-10,0,0) rot=(0.57735,0.57735,0.57735;2.0944rad)
  sketch-geometry (4):
    g0: LineSegment StartX=-18.0053 StartY=169.38 StartZ=0 EndX=-18.0053 EndY=160.38 EndZ=0
    g1: LineSegment StartX=-18.0053 StartY=160.38 StartZ=0 EndX=-7.00531 EndY=160.38 EndZ=0
    g2: LineSegment StartX=-7.00531 StartY=160.38 StartZ=0 EndX=-7.00531 EndY=169.38 EndZ=0
    g3: LineSegment StartX=-7.00531 StartY=169.38 StartZ=0 EndX=-18.0053 EndY=169.38 EndZ=0
  constraints (12):
    c: Coincident(g0,g1)
    c: Coincident(g1,g2)
    c: Coincident(g2,g3)
    c: Coincident(g3,g0)
    c: Vertical(g0)
    c: Vertical(g2)
    c: Horizontal(g1)
    c: Horizontal(g3)
    c: DistanceY(g0,g0) = 9
    c: Distance(g-6,g1) = 8
    c: DistanceX(g3,g3) = 11
    c: Distance(g0,g-7) = 8.85
FEATURE [Part::Extrusion] Extrude021  label="Left-Mag-Arm-Screwin-Part1"
  Base = -> Sketch021
  Dir = (1,0,0)
  DirMode = 2
  FaceMakerClass = Part::FaceMakerBullseye
  FaceMakerMode = 3
  LengthFwd = 40
  LengthRev = 0
  Placement = pos=(0,1.6,0) rot=(0,0,1;0rad)
  Solid = true
  Symmetric = false
FEATURE [Sketcher::SketchObject] Sketch023
  ArcFitTolerance = 1e-06
  AttachmentSupport = -> [Fusion014]
  ExternalGeometry = -> [Fusion014]
  FullyConstrained = true
  MakeInternals = false
  MapMode = 5
  Placement = pos=(0,-25.1552,0) rot=(1,0,0;1.5708rad)
  sketch-geometry (4):
    g0: LineSegment StartX=-18 StartY=237.88 StartZ=0 EndX=-18 EndY=226.88 EndZ=0
    g1: LineSegment StartX=-18 StartY=226.88 StartZ=0 EndX=-13.52 EndY=226.88 EndZ=0
    g2: LineSegment StartX=-13.52 StartY=226.88 StartZ=0 EndX=-13.52 EndY=237.88 EndZ=0
    g3: LineSegment StartX=-13.52 StartY=237.88 StartZ=0 EndX=-18 EndY=237.88 EndZ=0
  constraints (12):
    c: Coincident(g0,g1)
    c: Coincident(g1,g2)
    c: Coincident(g2,g3)
    c: Coincident(g3,g0)
    c: Vertical(g0)
    c: Vertical(g2)
    c: Horizontal(g1)
    c: Horizontal(g3)
    c: PointOnObject(g0,g-4)
    c: DistanceY(g2,g2) = 11
    c: DistanceX(g1,g1) = 4.48
    c: Distance(g3,g-3) = 10
FEATURE [Part::Extrusion] Extrude026
  Base = -> Sketch023
  Dir = (0,-1,2e-16)
  DirMode = 2
  FaceMakerClass = Part::FaceMakerBullseye
  FaceMakerMode = 3
  LengthFwd = 11
  LengthRev = 0
  Solid = true
  Symmetric = false
FEATURE [Sketcher::SketchObject] Sketch024
  ArcFitTolerance = 1e-06
  AttachmentSupport = -> [Extrude026]
  ExternalGeometry = -> [Fusion014,Extrude026]
  FullyConstrained = true
  MakeInternals = false
  MapMode = 5
  Placement = pos=(-13.52,0,0) rot=(0.57735,0.57735,0.57735;2.0944rad)
  sketch-geometry (2):
    g0: Circle CenterX=-30.6552 CenterY=232.38 CenterZ=0 NormalX=0 NormalY=0 NormalZ=1 AngleXU=0 Radius=1.375
    g1: Circle [constr] CenterX=-30.6552 CenterY=232.38 CenterZ=0 NormalX=0 NormalY=0 NormalZ=1 AngleXU=0 Radius=2.75
  constraints (6):
    c: Diameter(g0) = 2.75
    c: Diameter(g1) = 5.5
    c: Distance(g0,g-6) = 5.5
    c: Distance(g1,g-6) = 5.5
    c: Distance(g1,g-3) = 5.5
    c: Distance(g0,g-3) = 5.5
FEATURE [Part::Extrusion] Extrude027
  Base = -> Sketch024
  Dir = (1,0,0)
  DirMode = 2
  FaceMakerClass = Part::FaceMakerBullseye
  FaceMakerMode = 3
  LengthFwd = 0
  LengthRev = 5
  Solid = true
  Symmetric = false
FEATURE [Part::Cut] Cut009
  Base = -> Extrude026
  Tool = -> Extrude027
FEATURE [Part::Chamfer] Chamfer001  label="Left-Mag-Screwin-Front"
  Base = -> Cut009
  EdgeLinks = -> Cut009 [Edge6,Edge8,Edge11,Edge12,Edge13]
  Edges = 5 edges r=0.5: [Edge6,Edge8,Edge11,Edge12,Edge13]
FEATURE [Sketcher::SketchObject] Sketch026  label="Mag-Screwhole-back-left-sketch"
  ArcFitTolerance = 1e-06
  AttachmentSupport = -> [Fusion015]
  ExternalGeometry = -> [Fusion015]
  FullyConstrained = true
  MakeInternals = false
  MapMode = 5
  Placement = pos=(-23,0,0) rot=(0.57735,-0.57735,-0.57735;2.0944rad)
  sketch-geometry (4):
    g0: LineSegment StartX=-52.8448 StartY=169.88 StartZ=0 EndX=-52.8448 EndY=179.88 EndZ=0
    g1: LineSegment StartX=-52.8448 StartY=179.88 StartZ=0 EndX=-65.2948 EndY=179.88 EndZ=0
    g2: LineSegment StartX=-65.2948 StartY=179.88 StartZ=0 EndX=-65.2948 EndY=169.88 EndZ=0
    g3: LineSegment StartX=-65.2948 StartY=169.88 StartZ=0 EndX=-52.8448 EndY=169.88 EndZ=0
  constraints (10):
    c: Coincident(g0,g1)
    c: Coincident(g1,g2)
    c: Coincident(g2,g3)
    c: Coincident(g3,g0)
    c: Vertical(g0)
    c: Vertical(g2)
    c: Horizontal(g1)
    c: Horizontal(g3)
    c: Coincident(g0,g-4)
    c: Coincident(g1,g-6)
FEATURE [Sketcher::SketchObject] Sketch027  label="Mag-Screwhole-back-sketch"
  ArcFitTolerance = 1e-06
  AttachmentSupport = -> [Fusion015]
  ExternalGeometry = -> [Fusion015]
  FullyConstrained = true
  MakeInternals = false
  MapMode = 5
  Placement = pos=(-23,0,0) rot=(0.57735,-0.57735,-0.57735;2.0944rad)
  sketch-geometry (1):
    g0: Circle CenterX=-59.0947 CenterY=174.88 CenterZ=0 NormalX=0 NormalY=0 NormalZ=1 AngleXU=0 Radius=1.375
  constraints (3):
    c: Diameter(g0) = 2.75
    c: Distance(g0,g-4) = 5
    c: Distance(g0,g-3) = 6.225
FEATURE [Part::Extrusion] Extrude028  label="Mag-Screwhole-back"
  Base = -> Sketch027
  Dir = (-1,0,0)
  DirMode = 2
  FaceMakerClass = Part::FaceMakerBullseye
  FaceMakerMode = 3
  LengthFwd = 0
  LengthRev = 10
  Solid = true
  Symmetric = false
FEATURE [Part::Extrusion] Extrude029  label="Mag-Screwhole-back-left"
  Base = -> Sketch026
  Dir = (-1,0,0)
  DirMode = 2
  FaceMakerClass = Part::FaceMakerBullseye
  FaceMakerMode = 3
  LengthFwd = 0
  LengthRev = 5
  Placement = pos=(5,0,0) rot=(0,0,1;0rad)
  Solid = true
  Symmetric = false
FEATURE [Part::Chamfer] Chamfer002  label="Mag-Screwhole-back-left-rounded"
  Base = -> Extrude029
  EdgeLinks = -> Extrude029 [Edge5,Edge6,Edge9]
  Edges = 3 edges r=0.5: [Edge5,Edge6,Edge9]
FEATURE [Part::Cut] Cut010  label="Mag-Screwhole-back-left-rounded-with-hole"
  Base = -> Chamfer002
  Tool = -> Extrude028
FEATURE [Part::Cut] Cut011  label="Right-Mag-with-back-screwhole"
  Base = -> Fusion015
  Tool = -> Extrude028
FEATURE [Part::Fuse] Fusion017  label="Left-Mag-with-back-screwhole"
  Base = -> Fusion014
  Tool = -> Cut010
FEATURE [Sketcher::SketchObject] Sketch028
  ArcFitTolerance = 1e-06
  AttachmentSupport = -> [Chamfer001]
  ExternalGeometry = -> [Chamfer001,Cut009]
  FullyConstrained = true
  MakeInternals = false
  MapMode = 5
  Placement = pos=(-18,0,0) rot=(0.57735,-0.57735,-0.57735;2.0944rad)
  sketch-geometry (5):
    g0: LineSegment StartX=25.1552 StartY=237.88 StartZ=0 EndX=25.1552 EndY=226.88 EndZ=0
    g1: LineSegment StartX=25.1552 StartY=226.88 StartZ=0 EndX=36.1552 EndY=226.88 EndZ=0
    g2: LineSegment StartX=36.1552 StartY=226.88 StartZ=0 EndX=36.1552 EndY=237.88 EndZ=0
    g3: LineSegment StartX=36.1552 StartY=237.88 StartZ=0 EndX=25.1552 EndY=237.88 EndZ=0
    g4: Circle CenterX=30.6552 CenterY=232.38 CenterZ=0 NormalX=0 NormalY=0 NormalZ=1 AngleXU=0 Radius=1.375
  constraints (12):
    c: Coincident(g0,g1)
    c: Coincident(g1,g2)
    c: Coincident(g2,g3)
    c: Coincident(g3,g0)
    c: Vertical(g0)
    c: Vertical(g2)
    c: Horizontal(g1)
    c: Horizontal(g3)
    c: Coincident(g0,g-5)
    c: Coincident(g1,g-7)
    c: Coincident(g4,g-4)
    c: Equal(g4,g-4)
FEATURE [Sketcher::SketchObject] Sketch029
  ArcFitTolerance = 1e-06
  AttachmentSupport = -> [Cut011]
  ExternalGeometry = -> [Cut011]
  FullyConstrained = true
  MakeInternals = false
  MapMode = 5
  Placement = pos=(0,0,151.88) rot=(1,0,0;3.14159rad)
  sketch-geometry (4):
    g0: LineSegment StartX=-18 StartY=-0.344777 StartZ=0 EndX=-23 EndY=-0.344777 EndZ=0
    g1: LineSegment StartX=-23 StartY=-0.344777 StartZ=0 EndX=-23 EndY=-11.3448 EndZ=0
    g2: LineSegment StartX=-23 StartY=-11.3448 StartZ=0 EndX=-18 EndY=-11.3448 EndZ=0
    g3: LineSegment StartX=-18 StartY=-11.3448 StartZ=0 EndX=-18 EndY=-0.344777 EndZ=0
  constraints (12):
    c: Coincident(g0,g1)
    c: Coincident(g1,g2)
    c: Coincident(g2,g3)
    c: Coincident(g3,g0)
    c: Horizontal(g0)
    c: Horizontal(g2)
    c: Vertical(g1)
    c: Vertical(g3)
    c: PointOnObject(g0,g-4)
    c: DistanceY(g1,g1) = 11
    c: DistanceX(g2,g2) = 5
    c: Distance(g-6,g2) = 18.4313
FEATURE [Part::Extrusion] Extrude032  label="Right-Mag-Bottom-Screwin"
  Base = -> Sketch029
  Dir = (0,0,-1)
  DirMode = 2
  FaceMakerClass = Part::FaceMakerBullseye
  FaceMakerMode = 3
  LengthFwd = 11
  LengthRev = 0
  Solid = true
  Symmetric = false
FEATURE [Sketcher::SketchObject] Sketch030
  ArcFitTolerance = 1e-06
  AttachmentSupport = -> [Extrude032]
  ExternalGeometry = -> [Extrude032]
  FullyConstrained = true
  MakeInternals = false
  MapMode = 5
  Placement = pos=(-18,0,0) rot=(0.57735,0.57735,0.57735;2.0944rad)
  sketch-geometry (4):
    g0: LineSegment StartX=0.344777 StartY=151.88 StartZ=0 EndX=0.344777 EndY=140.88 EndZ=0
    g1: LineSegment StartX=0.344777 StartY=140.88 StartZ=0 EndX=11.3448 EndY=140.88 EndZ=0
    g2: LineSegment StartX=11.3448 StartY=140.88 StartZ=0 EndX=11.3448 EndY=151.88 EndZ=0
    g3: LineSegment StartX=11.3448 StartY=151.88 StartZ=0 EndX=0.344777 EndY=151.88 EndZ=0
  constraints (10):
    c: Coincident(g0,g1)
    c: Coincident(g1,g2)
    c: Coincident(g2,g3)
    c: Coincident(g3,g0)
    c: Vertical(g0)
    c: Vertical(g2)
    c: Horizontal(g1)
    c: Horizontal(g3)
    c: Coincident(g0,g-3)
    c: Coincident(g1,g-5)
FEATURE [Part::Extrusion] Extrude033
  Base = -> Sketch030
  Dir = (1,0,0)
  DirMode = 2
  FaceMakerClass = Part::FaceMakerBullseye
  FaceMakerMode = 3
  LengthFwd = 7
  LengthRev = 0
  Solid = true
  Symmetric = false
FEATURE [Part::Chamfer] Chamfer004  label="Left-Mag-Bottom-Screwin"
  Base = -> Extrude033
  EdgeLinks = -> Extrude033 [Edge2,Edge5]
  Edges = 2 edges r=0.5: [Edge2,Edge5]
FEATURE [Sketcher::SketchObject] Sketch031  label="Bottom-Screwin-Hole-Sketch "
  ArcFitTolerance = 1e-06
  AttachmentSupport = -> [Extrude032]
  ExternalGeometry = -> [Extrude032]
  FullyConstrained = true
  MakeInternals = false
  MapMode = 5
  Placement = pos=(-23,0,0) rot=(0.57735,-0.57735,-0.57735;2.0944rad)
  sketch-geometry (1):
    g0: Circle CenterX=-5.84478 CenterY=146.38 CenterZ=0 NormalX=0 NormalY=0 NormalZ=1 AngleXU=0 Radius=1.375
  constraints (3):
    c: Diameter(g0) = 2.75
    c: Distance(g0,g-3) = 5.5
    c: Distance(g0,g-4) = 5.5
FEATURE [Part::Extrusion] Extrude034  label="Bottom-Screwin-Hole"
  Base = -> Sketch031
  Dir = (-1,0,0)
  DirMode = 2
  FaceMakerClass = Part::FaceMakerBullseye
  FaceMakerMode = 3
  LengthFwd = 0
  LengthRev = 10.5
  Solid = true
  Symmetric = false
FEATURE [Part::Cut] Cut012  label="Right-Mag-Bottom-Screwin001"
  Base = -> Extrude032
  Tool = -> Extrude034
FEATURE [Part::Cut] Cut013  label="Left-Mag-Bottom-Screwin001"
  Base = -> Chamfer004
  Tool = -> Extrude034
FEATURE [Part::Chamfer] Chamfer005  label="Right-Mag-Bottom-Screwin002"
  Base = -> Cut012
  EdgeLinks = -> Cut012 [Edge2,Edge4,Edge10,Edge11,Edge14]
  Edges = 5 edges r=0.5: [Edge2,Edge4,Edge10,Edge11,Edge14]
FEATURE [Sketcher::SketchObject] Sketch032
  ArcFitTolerance = 1e-06
  AttachmentSupport = -> [Cut011]
  ExternalGeometry = -> [Cut011]
  FullyConstrained = true
  MakeInternals = false
  MapMode = 5
  Placement = pos=(0,52.8448,0) rot=(0,0.707107,0.707107;3.14159rad)
  sketch-geometry (4):
    g0: LineSegment StartX=18 StartY=237.88 StartZ=0 EndX=18 EndY=226.88 EndZ=0
    g1: LineSegment StartX=18 StartY=226.88 StartZ=0 EndX=23 EndY=226.88 EndZ=0
    g2: LineSegment StartX=23 StartY=226.88 StartZ=0 EndX=23 EndY=237.88 EndZ=0
    g3: LineSegment StartX=23 StartY=237.88 StartZ=0 EndX=18 EndY=237.88 EndZ=0
  constraints (12):
    c: Coincident(g0,g1)
    c: Coincident(g1,g2)
    c: Coincident(g2,g3)
    c: Coincident(g3,g0)
    c: Vertical(g0)
    c: Vertical(g2)
    c: Horizontal(g1)
    c: Horizontal(g3)
    c: PointOnObject(g0,g-4)
    c: DistanceX(g3,g3) = 5
    c: DistanceY(g0,g0) = 11
    c: Distance(g-3,g3) = 10
FEATURE [Part::Extrusion] Extrude035  label="Right-Mag-Back-Screwin-2"
  Base = -> Sketch032
  Dir = (0,1,-2e-16)
  DirMode = 2
  FaceMakerClass = Part::FaceMakerBullseye
  FaceMakerMode = 3
  LengthFwd = 11
  LengthRev = 0
  Solid = true
  Symmetric = false
FEATURE [Sketcher::SketchObject] Sketch033
  ArcFitTolerance = 1e-06
  AttachmentSupport = -> [Extrude035]
  ExternalGeometry = -> [Extrude035]
  FullyConstrained = true
  MakeInternals = false
  MapMode = 5
  Placement = pos=(-23,0,0) rot=(0.57735,-0.57735,-0.57735;2.0944rad)
  sketch-geometry (1):
    g0: Circle CenterX=-58.3448 CenterY=232.38 CenterZ=0 NormalX=0 NormalY=0 NormalZ=1 AngleXU=0 Radius=1.375
  constraints (3):
    c: Diameter(g0) = 2.75
    c: Distance(g0,g-3) = 5.5
    c: Distance(g0,g-4) = 5.5
FEATURE [Part::Extrusion] Extrude036
  Base = -> Sketch033
  Dir = (-1,0,0)
  DirMode = 2
  FaceMakerClass = Part::FaceMakerBullseye
  FaceMakerMode = 3
  LengthFwd = 0
  LengthRev = 11
  Solid = true
  Symmetric = false
FEATURE [Sketcher::SketchObject] Sketch034
  ArcFitTolerance = 1e-06
  AttachmentSupport = -> [Extrude035]
  ExternalGeometry = -> [Extrude035]
  FullyConstrained = true
  MakeInternals = false
  MapMode = 5
  Placement = pos=(-18,0,0) rot=(0.57735,0.57735,0.57735;2.0944rad)
  sketch-geometry (4):
    g0: LineSegment StartX=52.8448 StartY=237.88 StartZ=0 EndX=52.8448 EndY=226.88 EndZ=0
    g1: LineSegment StartX=52.8448 StartY=226.88 StartZ=0 EndX=63.8448 EndY=226.88 EndZ=0
    g2: LineSegment StartX=63.8448 StartY=226.88 StartZ=0 EndX=63.8448 EndY=237.88 EndZ=0
    g3: LineSegment StartX=63.8448 StartY=237.88 StartZ=0 EndX=52.8448 EndY=237.88 EndZ=0
  constraints (10):
    c: Coincident(g0,g1)
    c: Coincident(g1,g2)
    c: Coincident(g2,g3)
    c: Coincident(g3,g0)
    c: Vertical(g0)
    c: Vertical(g2)
    c: Horizontal(g1)
    c: Horizontal(g3)
    c: Coincident(g0,g-3)
    c: Coincident(g1,g-5)
FEATURE [Part::Extrusion] Extrude037  label="Left-Mag-Back-Screwin-2"
  Base = -> Sketch034
  Dir = (1,0,0)
  DirMode = 2
  FaceMakerClass = Part::FaceMakerBullseye
  FaceMakerMode = 3
  LengthFwd = 5
  LengthRev = 0
  Solid = true
  Symmetric = false
FEATURE [Part::Cut] Cut014  label="Right-Mag-Back-Screwin-003"
  Base = -> Extrude035
  Tool = -> Extrude036
FEATURE [Part::Cut] Cut015  label="Left-Mag-Back-Screwin-003"
  Base = -> Extrude037
  Tool = -> Extrude036
FEATURE [Part::Chamfer] Chamfer006  label="Left-Mag-Back-Screwin"
  Base = -> Cut015
  EdgeLinks = -> Cut015 [Edge5,Edge7,Edge8,Edge10,Edge13]
  Edges = 5 edges r=0.5: [Edge5,Edge7,Edge8,Edge10,Edge13]
FEATURE [Part::Chamfer] Chamfer007  label="Right-Mag-Back-Screwin"
  Base = -> Cut014
  EdgeLinks = -> Cut014 [Edge6,Edge8,Edge11,Edge12,Edge13]
  Edges = 5 edges r=0.5: [Edge6,Edge8,Edge11,Edge12,Edge13]
FEATURE [Part::Extrusion] Extrude038  label="Right-Mag-Screwin-Front002"
  Base = -> Sketch028
  Dir = (-1,0,0)
  DirMode = 2
  FaceMakerClass = Part::FaceMakerBullseye
  FaceMakerMode = 3
  LengthFwd = 5.58
  LengthRev = 0
  Solid = true
  Symmetric = false
FEATURE [Part::Chamfer] Chamfer008  label="Right-Mag-Screwin-Front003"
  Base = -> Extrude038
  EdgeLinks = -> Extrude038 [Edge5,Edge7,Edge8,Edge10,Edge12]
  Edges = 5 edges r=0.5: [Edge5,Edge7,Edge8,Edge10,Edge12]
FEATURE [Part::Extrusion] Extrude039  label="Left-Mag-Arm-Screwin-Part003"
  Base = -> Sketch021
  Dir = (1,0,0)
  DirMode = 2
  FaceMakerClass = Part::FaceMakerBullseye
  FaceMakerMode = 3
  LengthFwd = 40
  LengthRev = 0
  Placement = pos=(-58.1,1.6,0) rot=(0,0,1;0rad)
  Solid = true
  Symmetric = false
FEATURE [Sketcher::SketchObject] Sketch037
  ArcFitTolerance = 1e-06
  AttachmentSupport = -> [Cut011]
  ExternalGeometry = -> [Extrude039,Cut011]
  FullyConstrained = true
  MakeInternals = false
  MapMode = 5
  Placement = pos=(-28,0,0) rot=(0.57735,-0.57735,-0.57735;2.0944rad)
  sketch-geometry (4):
    g0: LineSegment StartX=5.40531 StartY=160.38 StartZ=0 EndX=5.40531 EndY=152.38 EndZ=0
    g1: LineSegment StartX=5.40531 StartY=152.38 StartZ=0 EndX=16.4053 EndY=152.38 EndZ=0
    g2: LineSegment StartX=16.4053 StartY=152.38 StartZ=0 EndX=16.4053 EndY=160.38 EndZ=0
    g3: LineSegment StartX=16.4053 StartY=160.38 StartZ=0 EndX=5.40531 EndY=160.38 EndZ=0
  constraints (11):
    c: Coincident(g0,g1)
    c: Coincident(g1,g2)
    c: Coincident(g2,g3)
    c: Coincident(g3,g0)
    c: Vertical(g0)
    c: Vertical(g2)
    c: Horizontal(g1)
    c: Horizontal(g3)
    c: Coincident(g0,g-3)
    c: PointOnObject(g1,g-4)
    c: DistanceX(g3,g3) = 11
FEATURE [Sketcher::SketchObject] Sketch038
  ArcFitTolerance = 1e-06
  FullyConstrained = true
  MakeInternals = false
  MapMode = 5
  Placement = pos=(0,0,160.38) rot=(0,0,1;0rad)
  sketch-geometry (4):
    g0: LineSegment StartX=-28 StartY=-16.4053 StartZ=0 EndX=-28 EndY=-5.40531 EndZ=0
    g1: LineSegment StartX=-28 StartY=-5.40531 StartZ=0 EndX=-68 EndY=-5.40531 EndZ=0
    g2: LineSegment StartX=-68 StartY=-5.40531 StartZ=0 EndX=-68 EndY=-16.4053 EndZ=0
    g3: LineSegment StartX=-68 StartY=-16.4053 StartZ=0 EndX=-28 EndY=-16.4053 EndZ=0
  constraints (10):
    c: Coincident(g0,g1)
    c: Coincident(g1,g2)
    c: Coincident(g2,g3)
    c: Coincident(g3,g0)
    c: Vertical(g0)
    c: Vertical(g2)
    c: Horizontal(g1)
    c: Horizontal(g3)
    c: Coincident(g0,g-5)
    c: Coincident(g1,g-4)
FEATURE [Part::Extrusion] Extrude044
  Base = -> Sketch038
  Dir = (0,0,1)
  DirMode = 2
  FaceMakerClass = Part::FaceMakerBullseye
  FaceMakerMode = 3
  LengthFwd = 9
  LengthRev = 0
  Solid = true
  Symmetric = false
FEATURE [Sketcher::SketchObject] Sketch039
  ArcFitTolerance = 1e-06
  FullyConstrained = true
  MakeInternals = false
  MapMode = 5
  Placement = pos=(0,-5.40531,0) rot=(0,0.707107,0.707107;3.14159rad)
  sketch-geometry (3):
    g0: LineSegment StartX=28 StartY=160.38 StartZ=0 EndX=28 EndY=152.38 EndZ=0
    g1: LineSegment StartX=28 StartY=152.38 StartZ=0 EndX=68 EndY=160.38 EndZ=0
    g2: LineSegment StartX=68 StartY=160.38 StartZ=0 EndX=28 EndY=160.38 EndZ=0
  constraints (6):
    c: Coincident(g-4,g0)
    c: Coincident(g0,g-3)
    c: Coincident(g0,g1)
    c: Coincident(g1,g-4)
    c: Coincident(g1,g2)
    c: Coincident(g2,g0)
FEATURE [Part::Extrusion] Extrude046
  Base = -> Sketch039
  Dir = (0,1,-2e-16)
  DirMode = 2
  FaceMakerClass = Part::FaceMakerBullseye
  FaceMakerMode = 3
  LengthFwd = 0
  LengthRev = 11
  Solid = true
  Symmetric = false
FEATURE [Sketcher::SketchObject] Sketch040
  ArcFitTolerance = 1e-06
  AttachmentSupport = -> [Extrude044]
  ExternalGeometry = -> [Extrude044]
  FullyConstrained = true
  MakeInternals = false
  MapMode = 5
  Placement = pos=(0,0,169.38) rot=(0,0,1;0rad)
  sketch-geometry (8):
    g0: LineSegment StartX=-68 StartY=-16.4053 StartZ=0 EndX=-57 EndY=-16.4053 EndZ=0
    g1: LineSegment StartX=-57 StartY=-16.4053 StartZ=0 EndX=-57 EndY=-11.4053 EndZ=0
    g2: LineSegment StartX=-57 StartY=-11.4053 StartZ=0 EndX=-68 EndY=-11.4053 EndZ=0
    g3: LineSegment StartX=-68 StartY=-11.4053 StartZ=0 EndX=-68 EndY=-16.4053 EndZ=0
    g4: LineSegment StartX=-28 StartY=-16.4053 StartZ=0 EndX=-28 EndY=-11.4053 EndZ=0
    g5: LineSegment StartX=-28 StartY=-11.4053 StartZ=0 EndX=-39 EndY=-11.4053 EndZ=0
    g6: LineSegment StartX=-39 StartY=-11.4053 StartZ=0 EndX=-39 EndY=-16.4053 EndZ=0
    g7: LineSegment StartX=-39 StartY=-16.4053 StartZ=0 EndX=-28 EndY=-16.4053 EndZ=0
  constraints (22):
    c: Coincident(g0,g1)
    c: Coincident(g1,g2)
    c: Coincident(g2,g3)
    c: Coincident(g3,g0)
    c: Horizontal(g0)
    c: Horizontal(g2)
    c: Vertical(g1)
    c: Vertical(g3)
    c: Coincident(g0,g-4)
    c: Coincident(g4,g5)
    c: Coincident(g5,g6)
    c: Coincident(g6,g7)
    c: Coincident(g7,g4)
    c: Vertical(g4)
    c: Vertical(g6)
    c: Horizontal(g5)
    c: Horizontal(g7)
    c: Coincident(g4,g-5)
    c: DistanceX(g2,g2) = 11
    c: DistanceY(g3,g3) = 5
    c: DistanceX(g5,g5) = 11
    c: DistanceY(g6,g6) = 5
FEATURE [Part::Extrusion] Extrude048
  Base = -> Sketch040
  Dir = (0,0,1)
  DirMode = 2
  FaceMakerClass = Part::FaceMakerBullseye
  FaceMakerMode = 3
  LengthFwd = 11
  LengthRev = 0
  Solid = true
  Symmetric = false
FEATURE [Sketcher::SketchObject] Sketch041
  ArcFitTolerance = 1e-06
  AttachmentSupport = -> [Extrude048]
  ExternalGeometry = -> [Extrude048]
  FullyConstrained = true
  MakeInternals = false
  MapMode = 5
  Placement = pos=(0,-11.4053,0) rot=(0,0.707107,0.707107;3.14159rad)
  sketch-geometry (2):
    g0: Circle CenterX=33.5 CenterY=174.88 CenterZ=0 NormalX=0 NormalY=0 NormalZ=1 AngleXU=0 Radius=1.375
    g1: Circle CenterX=62.5 CenterY=174.88 CenterZ=0 NormalX=0 NormalY=0 NormalZ=1 AngleXU=0 Radius=1.375
  constraints (6):
    c: Diameter(g0) = 2.75
    c: Diameter(g1) = 2.75
    c: Distance(g0,g-6) = 5.5
    c: Distance(g0,g-5) = 5.5
    c: Distance(g1,g-3) = 5.5
    c: Distance(g1,g-4) = 5.5
FEATURE [Part::Extrusion] Extrude049
  Base = -> Sketch041
  Dir = (0,1,-2e-16)
  DirMode = 2
  FaceMakerClass = Part::FaceMakerBullseye
  FaceMakerMode = 3
  LengthFwd = 0
  LengthRev = 12
  Solid = true
  Symmetric = false
FEATURE [Part::MultiFuse] Fusion018
  Shapes = -> [Extrude046,Extrude044,Extrude048]
FEATURE [Sketcher::SketchObject] Sketch042
  ArcFitTolerance = 1e-06
  AttachmentSupport = -> [Fusion018]
  ExternalGeometry = -> [Fusion018]
  FullyConstrained = true
  MakeInternals = false
  MapMode = 5
  Placement = pos=(-28,0,0) rot=(0.57735,0.57735,0.57735;2.0944rad)
  sketch-geometry (7):
    g0: LineSegment StartX=-16.4053 StartY=180.38 StartZ=0 EndX=-11.4053 EndY=180.38 EndZ=0
    g1: LineSegment StartX=-11.4053 StartY=180.38 StartZ=0 EndX=-11.4053 EndY=169.38 EndZ=0
    g2: LineSegment StartX=-11.4053 StartY=169.38 StartZ=0 EndX=-5.40531 EndY=169.38 EndZ=0
    g3: LineSegment StartX=-5.40531 StartY=169.38 StartZ=0 EndX=-5.40531 EndY=166.68 EndZ=0
    g4: LineSegment StartX=-5.40531 StartY=166.68 StartZ=0 EndX=-16.4053 EndY=166.68 EndZ=0
    g5: LineSegment StartX=-16.4053 StartY=166.68 StartZ=0 EndX=-16.4053 EndY=169.38 EndZ=0
    g6: LineSegment StartX=-16.4053 StartY=169.38 StartZ=0 EndX=-16.4053 EndY=180.38 EndZ=0
  constraints (16):
    c: Coincident(g-4,g0)
    c: Coincident(g0,g-5)
    c: Coincident(g0,g1)
    c: Coincident(g1,g-7)
    c: Coincident(g1,g2)
    c: Coincident(g2,g-8)
    c: Coincident(g2,g3)
    c: PointOnObject(g3,g-8)
    c: Coincident(g3,g4)
    c: PointOnObject(g4,g-6)
    c: Horizontal(g4)
    c: Coincident(g4,g5)
    c: Coincident(g5,g-6)
    c: Coincident(g5,g6)
    c: Coincident(g6,g0)
    c: DistanceY(g5,g5) = 2.7
FEATURE [Part::Extrusion] Extrude050
  Base = -> Sketch042
  Dir = (1,0,0)
  DirMode = 2
  FaceMakerClass = Part::FaceMakerBullseye
  FaceMakerMode = 3
  LengthFwd = 2
  LengthRev = 0
  Solid = true
  Symmetric = false
FEATURE [Sketcher::SketchObject] Sketch043
  ArcFitTolerance = 1e-06
  AttachmentSupport = -> [Extrude050]
  ExternalGeometry = -> [Extrude050]
  FullyConstrained = true
  MakeInternals = false
  MapMode = 5
  Placement = pos=(0,-16.4053,0) rot=(1,0,0;1.5708rad)
  sketch-geometry (4):
    g0: LineSegment StartX=-28 StartY=180.38 StartZ=0 EndX=-28 EndY=166.68 EndZ=0
    g1: LineSegment StartX=-28 StartY=166.68 StartZ=0 EndX=-26 EndY=166.68 EndZ=0
    g2: LineSegment StartX=-26 StartY=166.68 StartZ=0 EndX=-26 EndY=180.38 EndZ=0
    g3: LineSegment StartX=-26 StartY=180.38 StartZ=0 EndX=-28 EndY=180.38 EndZ=0
  constraints (10):
    c: Coincident(g0,g1)
    c: Coincident(g1,g2)
    c: Coincident(g2,g3)
    c: Coincident(g3,g0)
    c: Vertical(g0)
    c: Vertical(g2)
    c: Horizontal(g1)
    c: Horizontal(g3)
    c: Coincident(g0,g-3)
    c: Coincident(g1,g-6)
FEATURE [Part::Extrusion] Extrude052
  Base = -> Sketch043
  Dir = (0,-1,2e-16)
  DirMode = 2
  FaceMakerClass = Part::FaceMakerBullseye
  FaceMakerMode = 3
  LengthFwd = 3
  LengthRev = 0
  Solid = true
  Symmetric = false
FEATURE [Part::MultiFuse] Fusion019
  Shapes = -> [Extrude052,Extrude050]
FEATURE [Part::MultiFuse] Fusion020
  Shapes = -> [Fusion018,Fusion019]
FEATURE [Sketcher::SketchObject] Sketch044
  ArcFitTolerance = 1e-06
  AttachmentSupport = -> [Extrude021]
  ExternalGeometry = -> [Extrude021]
  FullyConstrained = true
  MakeInternals = false
  MapMode = 5
  Placement = pos=(0,1.6,160.38) rot=(1,0,0;3.14159rad)
  sketch-geometry (4):
    g0: LineSegment StartX=30 StartY=7.00531 StartZ=0 EndX=30 EndY=18.0053 EndZ=0
    g1: LineSegment StartX=30 StartY=18.0053 StartZ=0 EndX=-10 EndY=18.0053 EndZ=0
    g2: LineSegment StartX=-10 StartY=18.0053 StartZ=0 EndX=-10 EndY=7.00531 EndZ=0
    g3: LineSegment StartX=-10 StartY=7.00531 StartZ=0 EndX=30 EndY=7.00531 EndZ=0
  constraints (10):
    c: Coincident(g0,g1)
    c: Coincident(g1,g2)
    c: Coincident(g2,g3)
    c: Coincident(g3,g0)
    c: Vertical(g0)
    c: Vertical(g2)
    c: Horizontal(g1)
    c: Horizontal(g3)
    c: Coincident(g0,g-4)
    c: Coincident(g1,g-5)
FEATURE [Part::Extrusion] Extrude053
  Base = -> Sketch044
  Dir = (0,0,-1)
  DirMode = 2
  FaceMakerClass = Part::FaceMakerBullseye
  FaceMakerMode = 3
  LengthFwd = 7.5
  LengthRev = 0
  Solid = true
  Symmetric = false
FEATURE [Sketcher::SketchObject] Sketch045
  ArcFitTolerance = 1e-06
  AttachmentSupport = -> [Extrude053]
  ExternalGeometry = -> [Extrude021,Extrude053]
  FullyConstrained = true
  MakeInternals = false
  MapMode = 5
  Placement = pos=(0,-5.40531,0) rot=(0,0.707107,0.707107;3.14159rad)
  sketch-geometry (3):
    g0: LineSegment StartX=-30 StartY=160.38 StartZ=0 EndX=10 EndY=160.38 EndZ=0
    g1: LineSegment StartX=10 StartY=160.38 StartZ=0 EndX=10 EndY=152.88 EndZ=0
    g2: LineSegment StartX=10 StartY=152.88 StartZ=0 EndX=-30 EndY=160.38 EndZ=0
  constraints (6):
    c: Coincident(g-3,g0)
    c: Coincident(g0,g-4)
    c: Coincident(g0,g1)
    c: Coincident(g1,g-4)
    c: Coincident(g1,g2)
    c: Coincident(g2,g0)
FEATURE [Part::Extrusion] Extrude054
  Base = -> Sketch045
  Dir = (0,1,-2e-16)
  DirMode = 2
  FaceMakerClass = Part::FaceMakerBullseye
  FaceMakerMode = 3
  LengthFwd = 0
  LengthRev = 11
  Solid = true
  Symmetric = false
FEATURE [Sketcher::SketchObject] Sketch046
  ArcFitTolerance = 1e-06
  AttachmentSupport = -> [Extrude021]
  ExternalGeometry = -> [Extrude021]
  FullyConstrained = true
  MakeInternals = false
  MapMode = 5
  Placement = pos=(0,1.6,169.38) rot=(0,0,1;0rad)
  sketch-geometry (8):
    g0: LineSegment StartX=-10 StartY=-18.0053 StartZ=0 EndX=1 EndY=-18.0053 EndZ=0
    g1: LineSegment StartX=1 StartY=-18.0053 StartZ=0 EndX=1 EndY=-13.0053 EndZ=0
    g2: LineSegment StartX=1 StartY=-13.0053 StartZ=0 EndX=-10 EndY=-13.0053 EndZ=0
    g3: LineSegment StartX=-10 StartY=-13.0053 StartZ=0 EndX=-10 EndY=-18.0053 EndZ=0
    g4: LineSegment StartX=30 StartY=-18.0053 StartZ=0 EndX=30 EndY=-13.0053 EndZ=0
    g5: LineSegment StartX=30 StartY=-13.0053 StartZ=0 EndX=19 EndY=-13.0053 EndZ=0
    g6: LineSegment StartX=19 StartY=-13.0053 StartZ=0 EndX=19 EndY=-18.0053 EndZ=0
    g7: LineSegment StartX=19 StartY=-18.0053 StartZ=0 EndX=30 EndY=-18.0053 EndZ=0
  constraints (22):
    c: Coincident(g0,g1)
    c: Coincident(g1,g2)
    c: Coincident(g2,g3)
    c: Coincident(g3,g0)
    c: Horizontal(g0)
    c: Horizontal(g2)
    c: Vertical(g1)
    c: Vertical(g3)
    c: Coincident(g0,g-6)
    c: Coincident(g4,g5)
    c: Coincident(g5,g6)
    c: Coincident(g6,g7)
    c: Coincident(g7,g4)
    c: Vertical(g4)
    c: Vertical(g6)
    c: Horizontal(g5)
    c: Horizontal(g7)
    c: Coincident(g4,g-5)
    c: DistanceX(g2,g2) = 11
    c: DistanceX(g5,g5) = 11
    c: DistanceY(g1,g1) = 5
    c: DistanceY(g6,g6) = 5
FEATURE [Part::Extrusion] Extrude055
  Base = -> Sketch046
  Dir = (0,0,1)
  DirMode = 2
  FaceMakerClass = Part::FaceMakerBullseye
  FaceMakerMode = 3
  LengthFwd = 11
  LengthRev = 0
  Solid = true
  Symmetric = false
FEATURE [Part::MultiFuse] Fusion021
  Shapes = -> [Extrude021,Extrude054,Extrude055]
FEATURE [Sketcher::SketchObject] Sketch047
  ArcFitTolerance = 1e-06
  AttachmentSupport = -> [Fusion021]
  ExternalGeometry = -> [Fusion021]
  FullyConstrained = true
  MakeInternals = false
  MapMode = 5
  Placement = pos=(-10,0,0) rot=(0.57735,-0.57735,-0.57735;2.0944rad)
  sketch-geometry (7):
    g0: LineSegment StartX=16.4053 StartY=180.38 StartZ=0 EndX=11.4053 EndY=180.38 EndZ=0
    g1: LineSegment StartX=11.4053 StartY=180.38 StartZ=0 EndX=11.4053 EndY=169.38 EndZ=0
    g2: LineSegment StartX=11.4053 StartY=169.38 StartZ=0 EndX=5.40531 EndY=169.38 EndZ=0
    g3: LineSegment StartX=5.40531 StartY=169.38 StartZ=0 EndX=5.40531 EndY=166.63 EndZ=0
    g4: LineSegment StartX=5.40531 StartY=166.63 StartZ=0 EndX=16.4053 EndY=166.63 EndZ=0
    g5: LineSegment StartX=16.4053 StartY=166.63 StartZ=0 EndX=16.4053 EndY=169.38 EndZ=0
    g6: LineSegment StartX=16.4053 StartY=169.38 StartZ=0 EndX=16.4053 EndY=180.38 EndZ=0
  constraints (17):
    c: Coincident(g-7,g0)
    c: Coincident(g0,g-6)
    c: Coincident(g0,g1)
    c: Coincident(g1,g-5)
    c: Coincident(g1,g2)
    c: Coincident(g2,g-4)
    c: Coincident(g2,g3)
    c: PointOnObject(g3,g-3)
    c: Coincident(g3,g4)
    c: PointOnObject(g4,g-8)
    c: Horizontal(g4)
    c: Coincident(g4,g5)
    c: Coincident(g5,g-8)
    c: Coincident(g5,g6)
    c: PointOnObject(g6,g0)
    c: Vertical(g6)
    c: DistanceY(g3,g3) = 2.75
FEATURE [Part::Extrusion] Extrude056
  Base = -> Sketch047
  Dir = (-1,0,0)
  DirMode = 2
  FaceMakerClass = Part::FaceMakerBullseye
  FaceMakerMode = 3
  LengthFwd = 2
  LengthRev = 0
  Solid = true
  Symmetric = false
FEATURE [Sketcher::SketchObject] Sketch048
  ArcFitTolerance = 1e-06
  AttachmentSupport = -> [Extrude056]
  ExternalGeometry = -> [Extrude056]
  FullyConstrained = true
  MakeInternals = false
  MapMode = 5
  Placement = pos=(0,-16.4053,0) rot=(1,0,0;1.5708rad)
  sketch-geometry (4):
    g0: LineSegment StartX=-12 StartY=180.38 StartZ=0 EndX=-12 EndY=166.63 EndZ=0
    g1: LineSegment StartX=-12 StartY=166.63 StartZ=0 EndX=-10 EndY=166.63 EndZ=0
    g2: LineSegment StartX=-10 StartY=166.63 StartZ=0 EndX=-10 EndY=180.38 EndZ=0
    g3: LineSegment StartX=-10 StartY=180.38 StartZ=0 EndX=-12 EndY=180.38 EndZ=0
  constraints (10):
    c: Coincident(g0,g1)
    c: Coincident(g1,g2)
    c: Coincident(g2,g3)
    c: Coincident(g3,g0)
    c: Vertical(g0)
    c: Vertical(g2)
    c: Horizontal(g1)
    c: Horizontal(g3)
    c: Coincident(g0,g-4)
    c: Coincident(g1,g-6)
FEATURE [Part::Extrusion] Extrude057
  Base = -> Sketch048
  Dir = (0,-1,2e-16)
  DirMode = 2
  FaceMakerClass = Part::FaceMakerBullseye
  FaceMakerMode = 3
  LengthFwd = 3
  LengthRev = 0
  Solid = true
  Symmetric = false
FEATURE [Part::MultiFuse] Fusion022
  Shapes = -> [Fusion021,Extrude056,Extrude057]
FEATURE [Sketcher::SketchObject] Sketch049
  ArcFitTolerance = 1e-06
  AttachmentSupport = -> [Fusion022]
  ExternalGeometry = -> [Fusion022]
  FullyConstrained = true
  MakeInternals = false
  MapMode = 5
  Placement = pos=(0,-11.4053,0) rot=(0,0.707107,0.707107;3.14159rad)
  sketch-geometry (2):
    g0: Circle CenterX=-24.5 CenterY=174.88 CenterZ=0 NormalX=0 NormalY=0 NormalZ=1 AngleXU=0 Radius=1.375
    g1: Circle CenterX=4.5 CenterY=174.88 CenterZ=0 NormalX=0 NormalY=0 NormalZ=1 AngleXU=0 Radius=1.375
  constraints (6):
    c: Diameter(g0) = 2.75
    c: Diameter(g1) = 2.75
    c: Distance(g0,g-4) = 5.5
    c: Distance(g0,g-3) = 5.5
    c: Distance(g1,g-5) = 5.5
    c: Distance(g1,g-6) = 5.5
FEATURE [Part::Extrusion] Extrude058
  Base = -> Sketch049
  Dir = (0,1,-2e-16)
  DirMode = 2
  FaceMakerClass = Part::FaceMakerBullseye
  FaceMakerMode = 3
  LengthFwd = 0
  LengthRev = 12
  Solid = true
  Symmetric = false
FEATURE [Part::Cut] Cut016
  Base = -> Chamfer
  Tool = -> Extrude058
FEATURE [Part::Cut] Cut017  label="arm-final-smoothed-edges-screwholes"
  Base = -> Cut016
  Tool = -> Extrude049
FEATURE [Sketcher::SketchObject] Sketch050
  ArcFitTolerance = 1e-06
  AttachmentSupport = -> [Cut017]
  ExternalGeometry = -> [Cut017]
  FullyConstrained = true
  MakeInternals = false
  MapMode = 5
  Placement = pos=(0,0,173.5) rot=(0,0,1;0rad)
  sketch-geometry (4):
    g0: LineSegment StartX=28.7 StartY=-32 StartZ=0 EndX=28.7 EndY=-47 EndZ=0
    g1: LineSegment StartX=28.7 StartY=-47 StartZ=0 EndX=30.95 EndY=-47 EndZ=0
    g2: LineSegment StartX=30.95 StartY=-47 StartZ=0 EndX=30.95 EndY=-32 EndZ=0
    g3: LineSegment StartX=30.95 StartY=-32 StartZ=0 EndX=28.7 EndY=-32 EndZ=0
  constraints (10):
    c: Coincident(g0,g1)
    c: Coincident(g1,g2)
    c: Coincident(g2,g3)
    c: Coincident(g3,g0)
    c: Vertical(g0)
    c: Vertical(g2)
    c: Horizontal(g1)
    c: Horizontal(g3)
    c: Coincident(g0,g-6)
    c: Coincident(g1,g-5)
FEATURE [Part::Extrusion] Extrude059
  Base = -> Sketch050
  Dir = (0,0,1)
  DirMode = 2
  FaceMakerClass = Part::FaceMakerBullseye
  FaceMakerMode = 3
  LengthFwd = 0
  LengthRev = 4
  Solid = true
  Symmetric = false
FEATURE [Sketcher::SketchObject] Sketch051
  ArcFitTolerance = 1e-06
  AttachmentSupport = -> [Cut017]
  ExternalGeometry = -> [Cut017]
  FullyConstrained = true
  MakeInternals = false
  MapMode = 5
  Placement = pos=(0,0,173.5) rot=(0,0,1;0rad)
  sketch-geometry (4):
    g0: LineSegment StartX=-69.05 StartY=-32 StartZ=0 EndX=-69.05 EndY=-47 EndZ=0
    g1: LineSegment StartX=-69.05 StartY=-47 StartZ=0 EndX=-66.8 EndY=-47 EndZ=0
    g2: LineSegment StartX=-66.8 StartY=-47 StartZ=0 EndX=-66.8 EndY=-32 EndZ=0
    g3: LineSegment StartX=-66.8 StartY=-32 StartZ=0 EndX=-69.05 EndY=-32 EndZ=0
  constraints (10):
    c: Coincident(g0,g1)
    c: Coincident(g1,g2)
    c: Coincident(g2,g3)
    c: Coincident(g3,g0)
    c: Vertical(g0)
    c: Vertical(g2)
    c: Horizontal(g1)
    c: Horizontal(g3)
    c: Coincident(g0,g-5)
    c: Coincident(g1,g-6)
FEATURE [Part::Extrusion] Extrude060
  Base = -> Sketch051
  Dir = (0,0,1)
  DirMode = 2
  FaceMakerClass = Part::FaceMakerBullseye
  FaceMakerMode = 3
  LengthFwd = 0
  LengthRev = 4
  Solid = true
  Symmetric = false
FEATURE [Part::Cut] Cut018
  Base = -> Cut017
  Tool = -> Extrude059
FEATURE [Part::Cut] Cut019  label="arm-final-smoothed-edges-screwholes001"
  Base = -> Cut018
  Tool = -> Extrude060
FEATURE [Part::Cut] Cut020
  Base = -> Fusion020
  Tool = -> Extrude049
FEATURE [Part::Cut] Cut021
  Base = -> Fusion022
  Tool = -> Extrude058
FEATURE [Part::MultiFuse] Fusion023  label="Right-mag"
  Shapes = -> [Chamfer008,Chamfer007,Chamfer005,Cut011,Cut020]
FEATURE [Part::MultiFuse] Fusion024  label="Left-mag"
  Shapes = -> [Chamfer006,Chamfer001,Fusion017,Cut013,Cut021]
FEATURE [Part::Chamfer] Chamfer009
  Base = -> Fusion023
  EdgeLinks = -> Fusion023 [Edge761,Edge763,Edge764,Edge825,Edge827,Edge1769,Edge1770]
  Edges = 7 edges r=0.5: [Edge761,Edge763,Edge764,Edge825,Edge827,Edge1769,Edge1770]
FEATURE [Part::Chamfer] Chamfer010
  Base = -> Chamfer009
  EdgeLinks = -> Chamfer009 [Edge199,Edge200,Edge539,Edge546]
  Edges = 4 edges r=0.5: [Edge199,Edge200,Edge539,Edge546]
FEATURE [Part::Chamfer] Chamfer011  label="Right-mag-final"
  Base = -> Chamfer010
  EdgeLinks = -> Chamfer010 [Edge555,Edge556,Edge557,Edge922]
  Edges = 4 edges r=0.5: [Edge555,Edge556,Edge557,Edge922]
FEATURE [Part::Chamfer] Chamfer012  label="Left-mag-final"
  Base = -> Fusion024
  EdgeLinks = -> Fusion024 [Edge1098,Edge1099,Edge1100,Edge1101,Edge1103,Edge1105,Edge1117,Edge1119,Edge1884,Edge1894,Edge1898,Edge1902,Edge1906,Edge2493,Edge2496,Edge2498]
  Edges = 16 edges r=0.5: [Edge1098,Edge1099,Edge1100,Edge1101,Edge1103,Edge1105,Edge1117,Edge1119,Edge1884,Edge1894,Edge1898,Edge1902,Edge1906,Edge2493,Edge2496,Edge2498]
FEATURE [Mesh::Feature] Mesh  label="arm-mesh"
FEATURE [Mesh::Feature] Mesh001  label="left-mag-mesh"
FEATURE [Mesh::Feature] Mesh002  label="right-mag-mesh"
FEATURE [Sketcher::SketchObject] Sketch052
  ArcFitTolerance = 1e-06
  AttachmentSupport = -> [Cut019]
  ExternalGeometry = -> [Cut019]
  FullyConstrained = true
  MakeInternals = false
  MapMode = 5
  Placement = pos=(0,0,210) rot=(0,0,1;0rad)
  sketch-geometry (5):
    g0: LineSegment [constr] StartX=-21.55 StartY=-52 StartZ=0 EndX=-21.55 EndY=-61.5 EndZ=0
    g1: LineSegment [constr] StartX=-16.55 StartY=-52 StartZ=0 EndX=-16.55 EndY=-61.5 EndZ=0
    g2: LineSegment [constr] StartX=-21.55 StartY=-55.25 StartZ=0 EndX=-16.55 EndY=-55.25 EndZ=0
    g3: LineSegment [constr] StartX=-19.05 StartY=-52 StartZ=0 EndX=-19.05 EndY=-61.5 EndZ=0
    g4: Circle CenterX=-19.05 CenterY=-56 CenterZ=0 NormalX=0 NormalY=0 NormalZ=1 AngleXU=0 Radius=0.825
  constraints (17):
    c: PointOnObject(g0,g-6)
    c: PointOnObject(g0,g-4)
    c: Vertical(g0)
    c: Distance(g0,g-6) = 9.25
    c: PointOnObject(g1,g-6)
    c: PointOnObject(g1,g-4)
    c: Vertical(g1)
    c: Distance(g1,g-6) = 9.25
    c: PointOnObject(g2,g0)
    c: PointOnObject(g2,g1)
    c: Horizontal(g2)
    c: Distance(g2,g0) = 3.25
    c: Symmetric(g-6,g-6,g3)
    c: Symmetric(g-4,g-4,g3)
    c: PointOnObject(g4,g3)
    c: Diameter(g4) = 1.65
    c: Distance(g4,g3) = 4
FEATURE [Part::Extrusion] Extrude061
  Base = -> Sketch052
  Dir = (0,0,1)
  DirMode = 2
  FaceMakerClass = Part::FaceMakerBullseye
  FaceMakerMode = 3
  LengthFwd = -7
  LengthRev = 0
  Solid = true
  Symmetric = false
FEATURE [Part::Cut] Cut022  label="arm_with_screw_for_cam"
  Base = -> Cut019
  Refine = true
  Tool = -> Extrude061
FEATURE [Part::Box] Box002  label="Cube"
  AttacherType = Attacher::AttachEngine3D
  Height = 35
  Length = 37.05
  Placement = pos=(-69.05,-64,170) rot=(0,0,1;0rad)
  Width = 50
FEATURE [Part::Box] Box003  label="Cube001"
  AttacherType = Attacher::AttachEngine3D
  Height = 35
  Length = 37.05
  Placement = pos=(-6.1,-64,170) rot=(0,0,1;0rad)
  Width = 50
FEATURE [Part::Cut] Cut023
  Base = -> Cut022
  Refine = true
  Tool = -> Box002
FEATURE [Part::Cut] Cut024
  Base = -> Cut023
  Placement = pos=(0,-61.7,0) rot=(0,0,1;0rad)
  Refine = true
  Tool = -> Box003
FEATURE [Mesh::Feature] import_motor_mount
FEATURE [Part::Feature] import_motor_mount001
  shape: bbox 82 x 19.25 x 14.5 mm, 2056 faces, 0 solids (baked)
FEATURE [Part::Refine] import_motor_mount002
  Source = -> import_motor_mount001
FEATURE [Part::Feature] import_motor_mount002_solid  label="import_motor_mount002 (Solid)"
  shape: bbox 82 x 19.25 x 14.5 mm, 1352 faces (baked)
FEATURE [Part::Feature] Cut025
  Placement = pos=(0,-121.5,0) rot=(0,0,1;0rad)
  shape: bbox 25.9 x 45 x 40 mm, 2059 faces (baked)
FEATURE [Part::Box] Box004  label="Cube002"
  AttacherType = Attacher::AttachEngine3D
  Height = 50
  Length = 50
  Placement = pos=(-49.3,-173.5,163) rot=(0,0,1;0rad)
  Width = 80
FEATURE [Part::Feature] Cut026
  Placement = pos=(0,-121.5,0) rot=(0,0,1;0rad)
  shape: bbox 25.9 x 45 x 40 mm, 2059 faces (baked)
FEATURE [Part::Feature] Box005  label="Cube003"
  Placement = pos=(-49.3,-173,163) rot=(0,0,1;0rad)
  shape: bbox 50 x 21.75 x 50 mm, 6 faces (baked)
FEATURE [Part::Cut] Cut027  label="front_wall"
  Base = -> Cut025
  Placement = pos=(0,121.9,2.38) rot=(0,0,1;0rad)
  Refine = true
  Tool = -> Box004
FEATURE [Sketcher::SketchObject] Sketch053
  ArcFitTolerance = 1e-06
  AttachmentSupport = -> [Box005]
  ExternalGeometry = -> [Box005]
  FullyConstrained = true
  MakeInternals = false
  MapMode = 5
  Placement = pos=(-49.3,-173,163) rot=(1,0,0;1.5708rad)
  sketch-geometry (4):
    g0: LineSegment StartX=0 StartY=50 StartZ=0 EndX=0 EndY=0 EndZ=0
    g1: LineSegment StartX=0 StartY=0 StartZ=0 EndX=50 EndY=0 EndZ=0
    g2: LineSegment StartX=50 StartY=0 StartZ=0 EndX=50 EndY=50 EndZ=0
    g3: LineSegment StartX=50 StartY=50 StartZ=0 EndX=0 EndY=50 EndZ=0
  constraints (8):
    c: Coincident(g0,g-6)
    c: Coincident(g0,g-1)
    c: Coincident(g0,g1)
    c: Coincident(g1,g-5)
    c: Coincident(g1,g2)
    c: Coincident(g2,g-4)
    c: Coincident(g2,g3)
    c: Coincident(g3,g0)
FEATURE [Part::Extrusion] Extrude062
  Base = -> Sketch053
  Dir = (0,-1,2e-16)
  DirMode = 2
  FaceMakerClass = Part::FaceMakerBullseye
  FaceMakerMode = 3
  LengthFwd = 50
  LengthRev = 0
  Solid = true
  Symmetric = false
FEATURE [Part::MultiFuse] Fusion025
  Refine = true
  Shapes = -> [Box005,Extrude062]
FEATURE [Part::Cut] Cut028  label="back_mount"
  Base = -> Cut026
  Placement = pos=(0,121.6,-0.12) rot=(0,0,1;0rad)
  Refine = true
  Tool = -> Fusion025
FEATURE [Sketcher::SketchObject] Sketch054
  ArcFitTolerance = 1e-06
  AttachmentSupport = -> [import_motor_mount002_solid]
  ExternalGeometry = -> [import_motor_mount002_solid]
  FullyConstrained = true
  MakeInternals = false
  MapMode = 5
  Placement = pos=(0,-49.0302,0) rot=(1,0,0;1.5708rad)
  sketch-geometry (4):
    g0: LineSegment StartX=-25.8362 StartY=172.38 StartZ=0 EndX=-12.1638 EndY=172.38 EndZ=0
    g1: LineSegment StartX=-12.1638 StartY=172.38 StartZ=0 EndX=-12.1638 EndY=169.88 EndZ=0
    g2: LineSegment StartX=-12.1638 StartY=169.88 StartZ=0 EndX=-25.8362 EndY=169.88 EndZ=0
    g3: LineSegment StartX=-25.8362 StartY=172.38 StartZ=0 EndX=-25.8362 EndY=169.88 EndZ=0
  constraints (8):
    c: Coincident(g0,g-3)
    c: Coincident(g0,g-5)
    c: Coincident(g1,g0)
    c: Coincident(g1,g-5)
    c: Coincident(g2,g1)
    c: Coincident(g2,g-4)
    c: Coincident(g3,g0)
    c: Coincident(g3,g2)
FEATURE [Part::Extrusion] Extrude063
  Base = -> Sketch054
  Dir = (0,-1,2e-16)
  DirMode = 2
  FaceMakerClass = Part::FaceMakerBullseye
  FaceMakerMode = 3
  LengthFwd = 12.07
  LengthRev = 0
  Solid = true
  Symmetric = false
FEATURE [Part::MultiFuse] Fusion026
  Refine = true
  Shapes = -> [import_motor_mount002_solid,Extrude063]
FEATURE [Part::Box] Box006  label="Cube004"
  AttacherType = Attacher::AttachEngine3D
  Height = 2.5
  Length = 17
  Placement = pos=(-27.5,-62.7,169.88) rot=(0,0,1;0rad)
  Width = 13.67
FEATURE [Part::MultiFuse] Fusion027
  Refine = true
  Shapes = -> [Fusion026,Cut027]
FEATURE [Mesh::Feature] import_gyro_mount
FEATURE [Part::Feature] import_gyro_mount001
  shape: bbox 24.5 x 16.43 x 6 mm, 2640 faces, 0 solids (baked)
FEATURE [Part::Refine] import_gyro_mount002
  Source = -> import_gyro_mount001
FEATURE [Part::Feature] import_gyro_mount002_solid  label="import_gyro_mount002 (Solid)"
  Placement = pos=(0,-32.2,185.6) rot=(0,0,1;0rad)
  shape: bbox 24.5 x 16.43 x 6 mm, 2020 faces (baked)
FEATURE [Sketcher::SketchObject] Sketch055
  ArcFitTolerance = 1e-06
  AttachmentSupport = -> [Fusion027]
  ExternalGeometry = -> [Fusion027]
  FullyConstrained = true
  MakeInternals = false
  MapMode = 5
  Placement = pos=(0,-29.7802,0) rot=(0,0.707107,0.707107;3.14159rad)
  sketch-geometry (4):
    g0: LineSegment StartX=12.1638 StartY=172.38 StartZ=0 EndX=12.1638 EndY=169.88 EndZ=0
    g1: LineSegment StartX=12.1638 StartY=169.88 StartZ=0 EndX=25.8362 EndY=169.88 EndZ=0
    g2: LineSegment StartX=25.8362 StartY=169.88 StartZ=0 EndX=25.8362 EndY=172.38 EndZ=0
    g3: LineSegment StartX=25.8362 StartY=172.38 StartZ=0 EndX=12.1638 EndY=172.38 EndZ=0
  constraints (8):
    c: Coincident(g0,g-3)
    c: Coincident(g0,g-4)
    c: Coincident(g0,g1)
    c: Coincident(g1,g-5)
    c: Coincident(g1,g2)
    c: Coincident(g2,g-5)
    c: Coincident(g2,g3)
    c: Coincident(g3,g0)
FEATURE [Part::Extrusion] Extrude064
  Base = -> Sketch055
  Dir = (0,1,-2e-16)
  DirMode = 2
  FaceMakerClass = Part::FaceMakerBullseye
  FaceMakerMode = 3
  LengthFwd = 4.63
  LengthRev = 0
  Solid = true
  Symmetric = false
FEATURE [Part::MultiFuse] Fusion028
  Refine = true
  Shapes = -> [Extrude064,Fusion027]
FEATURE [Sketcher::SketchObject] Sketch056
  ArcFitTolerance = 1e-06
  AttachmentSupport = -> [Cut028]
  ExternalGeometry = -> [Cut028]
  FullyConstrained = true
  MakeInternals = false
  MapMode = 5
  Placement = pos=(0,-29.65,-0.12) rot=(1,0,0;1.5708rad)
  sketch-geometry (4):
    g0: LineSegment StartX=-32 StartY=200 StartZ=0 EndX=-6.1 EndY=200 EndZ=0
    g1: LineSegment StartX=-6.1 StartY=200 StartZ=0 EndX=-6.1 EndY=170 EndZ=0
    g2: LineSegment StartX=-6.1 StartY=170 StartZ=0 EndX=-32 EndY=170 EndZ=0
    g3: LineSegment StartX=-32 StartY=170 StartZ=0 EndX=-32 EndY=200 EndZ=0
  constraints (8):
    c: Coincident(g-4,g0)
    c: Coincident(g0,g-5)
    c: Coincident(g0,g1)
    c: Coincident(g1,g-6)
    c: Coincident(g1,g2)
    c: Coincident(g2,g-6)
    c: Coincident(g2,g3)
    c: Coincident(g3,g0)
FEATURE [Part::Extrusion] Extrude065
  Base = -> Sketch056
  Dir = (0,-1,2e-16)
  DirMode = 2
  FaceMakerClass = Part::FaceMakerBullseye
  FaceMakerMode = 3
  LengthFwd = 0.13
  LengthRev = 0
  Solid = true
  Symmetric = false
FEATURE [Part::MultiFuse] Fusion029
  Refine = true
  Shapes = -> [Extrude065,Cut028]
FEATURE [Part::MultiFuse] Fusion030
  Placement = pos=(0,-0.0003,0.0002) rot=(0,0,1;0rad)
  Refine = true
  Shapes = -> [Fusion028,Fusion029]
FEATURE [Part::Box] Box007  label="Cube005"
  AttacherType = Attacher::AttachEngine3D
  Height = 12.01
  Length = 20
  Placement = pos=(-29.4,-49.03,172.37) rot=(0,0,1;0rad)
  Width = 19.25
FEATURE [Part::Chamfer] Chamfer013
  Base = -> Box007
  EdgeLinks = -> Box007 [Edge11]
  Edges = 1 edges: [Edge11 r1=12 r2=19.24]
  Placement = pos=(0,-0.0005,0.0005) rot=(0,0,1;0rad)
FEATURE [Part::Cut] Cut029
  Base = -> Fusion030
  Refine = true
  Tool = -> Chamfer013
FEATURE [Sketcher::SketchObject] Sketch057
  ArcFitTolerance = 1e-06
  AttachmentSupport = -> [Cut029]
  ExternalGeometry = -> [Cut029]
  FullyConstrained = true
  MakeInternals = false
  MapMode = 5
  Placement = pos=(0,0,169.88) rot=(1,0,0;3.14159rad)
  sketch-geometry (14):
    g0: LineSegment StartX=-32 StartY=29.7803 StartZ=0 EndX=-25.84 EndY=29.7803 EndZ=0
    g1: LineSegment StartX=-6.1 StartY=29.7803 StartZ=0 EndX=-12.16 EndY=29.7803 EndZ=0
    g2: LineSegment StartX=-32 StartY=29.7803 StartZ=0 EndX=-32 EndY=17.4003 EndZ=0
    g3: LineSegment StartX=-32 StartY=16.9003 StartZ=0 EndX=-32 EndY=17.4003 EndZ=0
    g4: LineSegment StartX=-28.15 StartY=16.9003 StartZ=0 EndX=-32 EndY=16.9003 EndZ=0
    g5: LineSegment StartX=-28.15 StartY=17.4003 StartZ=0 EndX=-28.15 EndY=16.9003 EndZ=0
    g6: LineSegment StartX=-28.15 StartY=25.1503 StartZ=0 EndX=-28.15 EndY=17.4003 EndZ=0
    g7: LineSegment StartX=-9.95 StartY=25.1503 StartZ=0 EndX=-9.95 EndY=17.4003 EndZ=0
    g8: LineSegment StartX=-9.95 StartY=16.9003 StartZ=0 EndX=-9.95 EndY=17.4003 EndZ=0
    g9: LineSegment StartX=-9.95 StartY=16.9003 StartZ=0 EndX=-6.1 EndY=16.9003 EndZ=0
    g10: LineSegment StartX=-6.1 StartY=16.9003 StartZ=0 EndX=-6.1 EndY=17.4003 EndZ=0
    g11: LineSegment StartX=-6.1 StartY=17.4003 StartZ=0 EndX=-6.1 EndY=29.7803 EndZ=0
    g12: LineSegment StartX=-25.84 StartY=29.7803 StartZ=0 EndX=-28.15 EndY=25.1503 EndZ=0
    g13: LineSegment StartX=-12.16 StartY=29.7803 StartZ=0 EndX=-9.95 EndY=25.1503 EndZ=0
  constraints (30):
    c: Distance(g0) = 6.16
    c: Coincident(g0,g-3)
    c: Horizontal(g0)
    c: Distance(g1) = 6.06
    c: Coincident(g1,g-11)
    c: Horizontal(g1)
    c: Coincident(g2,g0)
    c: Coincident(g2,g-12)
    c: Coincident(g3,g-12)
    c: Coincident(g3,g2)
    c: Coincident(g4,g-6)
    c: Coincident(g4,g3)
    c: Coincident(g5,g-7)
    c: Coincident(g5,g4)
    c: Coincident(g6,g-7)
    c: Coincident(g6,g5)
    c: Coincident(g7,g-8)
    c: Coincident(g7,g-13)
    c: Coincident(g8,g-13)
    c: Coincident(g8,g7)
    c: Coincident(g8,g9)
    c: Coincident(g9,g-14)
    c: Coincident(g9,g10)
    c: Coincident(g10,g-11)
    c: Coincident(g10,g11)
    c: Coincident(g11,g1)
    c: Coincident(g12,g0)
    c: Coincident(g12,g6)
    c: Coincident(g13,g1)
    c: Coincident(g13,g7)
FEATURE [Part::Extrusion] Extrude066
  Base = -> Sketch057
  Dir = (0,0,-1)
  DirMode = 2
  FaceMakerClass = Part::FaceMakerBullseye
  FaceMakerMode = 3
  LengthFwd = -2.5
  LengthRev = 0
  Solid = true
  Symmetric = false
FEATURE [Part::Cut] Cut030
  Base = -> Cut029
  Refine = true
  Tool = -> Extrude066
FEATURE [Part::Box] Box008  label="Cube006"
  AttacherType = Attacher::AttachEngine3D
  Height = 50
  Length = 50
  Placement = pos=(-48.3,-133.6,165.4) rot=(0,0,1;0rad)
  Width = 20
FEATURE [Part::Box] Box009  label="Cube007"
  AttacherType = Attacher::AttachEngine3D
  Height = 50
  Length = 50
  Placement = pos=(-48.3,-92,165.4) rot=(0,0,1;0rad)
  Width = 20
FEATURE [Part::Cut] Cut031
  Base = -> Cut024
  Refine = true
  Tool = -> Box008
FEATURE [Part::Cut] Cut032
  Base = -> Cut031
  Refine = true
  Tool = -> Box009
FEATURE [Part::Box] Box010  label="Cube008"
  AttacherType = Attacher::AttachEngine3D
  Height = 50
  Length = 50
  Placement = pos=(-53.4,-115,146.2) rot=(0,0,1;0rad)
  Width = 50
FEATURE [Part::Cut] Cut033  label="top"
  Base = -> Cut032
  Placement = pos=(0,62,6.03) rot=(0,0,1;0rad)
  Refine = true
  Tool = -> Box010
FEATURE [Part::MultiFuse] Fusion031
  Refine = true
  Shapes = -> [Cut030,Cut033]
FEATURE [Sketcher::SketchObject] Sketch058
  ArcFitTolerance = 1e-06
  AttachmentSupport = -> [Fusion031]
  ExternalGeometry = -> [Fusion031]
  FullyConstrained = true
  MakeInternals = false
  MapMode = 5
  Placement = pos=(-6.1,0,0) rot=(0.57735,0.57735,0.57735;2.0944rad)
  sketch-geometry (4):
    g0: LineSegment StartX=-51.6 StartY=206.03 StartZ=0 EndX=-51.6 EndY=202.23 EndZ=0
    g1: LineSegment StartX=-51.6 StartY=202.23 StartZ=0 EndX=-30 EndY=202.23 EndZ=0
    g2: LineSegment StartX=-30 StartY=202.23 StartZ=0 EndX=-30 EndY=206.03 EndZ=0
    g3: LineSegment StartX=-30 StartY=206.03 StartZ=0 EndX=-51.6 EndY=206.03 EndZ=0
  constraints (8):
    c: Coincident(g-4,g0)
    c: Coincident(g0,g-5)
    c: Coincident(g0,g1)
    c: Coincident(g1,g-6)
    c: Coincident(g1,g2)
    c: Coincident(g2,g-6)
    c: Coincident(g2,g3)
    c: Coincident(g3,g0)
FEATURE [Part::Extrusion] Extrude067
  Base = -> Sketch058
  Dir = (1,0,0)
  DirMode = 2
  FaceMakerClass = Part::FaceMakerBullseye
  FaceMakerMode = 3
  LengthFwd = -0.7
  LengthRev = 0
  Solid = true
  Symmetric = false
FEATURE [Part::Cut] Cut034
  Base = -> Fusion031
  Refine = true
  Tool = -> Extrude067
FEATURE [Sketcher::SketchObject] Sketch059
  ArcFitTolerance = 1e-06
  AttachmentSupport = -> [Cut034]
  ExternalGeometry = -> [Cut034]
  FullyConstrained = true
  MakeInternals = false
  MapMode = 5
  Placement = pos=(-32,0,0) rot=(0.57735,-0.57735,-0.57735;2.0944rad)
  sketch-geometry (4):
    g0: LineSegment StartX=30 StartY=206.03 StartZ=0 EndX=30 EndY=202.23 EndZ=0
    g1: LineSegment StartX=30 StartY=202.23 StartZ=0 EndX=51.6 EndY=202.23 EndZ=0
    g2: LineSegment StartX=51.6 StartY=202.23 StartZ=0 EndX=51.6 EndY=206.03 EndZ=0
    g3: LineSegment StartX=51.6 StartY=206.03 StartZ=0 EndX=30 EndY=206.03 EndZ=0
  constraints (8):
    c: Coincident(g-4,g0)
    c: Coincident(g0,g-6)
    c: Coincident(g0,g1)
    c: Coincident(g1,g-6)
    c: Coincident(g1,g2)
    c: Coincident(g2,g-5)
    c: Coincident(g2,g3)
    c: Coincident(g3,g0)
FEATURE [Part::Extrusion] Extrude068
  Base = -> Sketch059
  Dir = (-1,0,0)
  DirMode = 2
  FaceMakerClass = Part::FaceMakerBullseye
  FaceMakerMode = 3
  LengthFwd = -0.7
  LengthRev = 0
  Solid = true
  Symmetric = false
FEATURE [Part::Cut] Cut035
  Base = -> Cut034
  Refine = true
  Tool = -> Extrude068
FEATURE [Sketcher::SketchObject] Sketch060
  ArcFitTolerance = 1e-06
  AttachmentSupport = -> [Cut035]
  ExternalGeometry = -> [Cut035]
  FullyConstrained = true
  MakeInternals = false
  MapMode = 5
  Placement = pos=(0,0,202.23) rot=(1,0,0;3.14159rad)
  sketch-geometry (8):
    g0: LineSegment StartX=-31.3 StartY=51.6 StartZ=0 EndX=-31.3 EndY=30 EndZ=0
    g1: LineSegment StartX=-31.3 StartY=30 StartZ=0 EndX=-27.5499 EndY=30 EndZ=0
    g2: LineSegment StartX=-27.5499 StartY=34.95 StartZ=0 EndX=-27.5499 EndY=30 EndZ=0
    g3: LineSegment StartX=-27.5499 StartY=34.95 StartZ=0 EndX=-10.5499 EndY=34.95 EndZ=0
    g4: LineSegment StartX=-10.5499 StartY=34.95 StartZ=0 EndX=-10.55 EndY=30 EndZ=0
    g5: LineSegment StartX=-10.55 StartY=30 StartZ=0 EndX=-6.8 EndY=30 EndZ=0
    g6: LineSegment StartX=-6.8 StartY=30 StartZ=0 EndX=-6.8 EndY=51.6 EndZ=0
    g7: LineSegment StartX=-6.8 StartY=51.6 StartZ=0 EndX=-31.3 EndY=51.6 EndZ=0
  constraints (17):
    c: Coincident(g-5,g0)
    c: Coincident(g0,g-5)
    c: Coincident(g0,g1)
    c: Coincident(g1,g-7)
    c: Coincident(g-7,g2)
    c: Coincident(g2,g1)
    c: Coincident(g2,g3)
    c: Coincident(g3,g-8)
    c: Coincident(g3,g4)
    c: Coincident(g4,g-8)
    c: Coincident(g4,g5)
    c: Coincident(g5,g-9)
    c: Coincident(g5,g6)
    c: Coincident(g6,g-4)
    c: Coincident(g6,g7)
    c: PointOnObject(g7,g0)
    c: Horizontal(g7)
FEATURE [Part::Extrusion] Extrude069
  Base = -> Sketch060
  Dir = (0,0,-1)
  DirMode = 2
  FaceMakerClass = Part::FaceMakerBullseye
  FaceMakerMode = 3
  LengthFwd = -0.15
  LengthRev = 0
  Solid = true
  Symmetric = false
FEATURE [Part::Cut] Cut036
  Base = -> Cut035
  Refine = true
  Tool = -> Extrude069
FEATURE [Sketcher::SketchObject] Sketch061
  ArcFitTolerance = 1e-06
  AttachmentSupport = -> [Cut036]
  ExternalGeometry = -> [Cut036]
  FullyConstrained = true
  MakeInternals = false
  MapMode = 5
  Placement = pos=(0,-30,0) rot=(0,0.707107,0.707107;3.14159rad)
  sketch-geometry (8):
    g0: LineSegment StartX=6.8 StartY=206.03 StartZ=0 EndX=10.55 EndY=206.03 EndZ=0
    g1: LineSegment StartX=10.55 StartY=206.03 StartZ=0 EndX=10.55 EndY=202.38 EndZ=0
    g2: LineSegment StartX=10.55 StartY=202.38 StartZ=0 EndX=6.8 EndY=202.38 EndZ=0
    g3: LineSegment StartX=6.8 StartY=202.38 StartZ=0 EndX=6.8 EndY=206.03 EndZ=0
    g4: LineSegment StartX=27.5499 StartY=206.03 StartZ=0 EndX=31.3 EndY=206.03 EndZ=0
    g5: LineSegment StartX=31.3 StartY=206.03 StartZ=0 EndX=31.3 EndY=202.38 EndZ=0
    g6: LineSegment StartX=31.3 StartY=202.38 StartZ=0 EndX=27.5499 EndY=202.38 EndZ=0
    g7: LineSegment StartX=27.5499 StartY=202.38 StartZ=0 EndX=27.5499 EndY=206.03 EndZ=0
  constraints (16):
    c: Coincident(g-4,g0)
    c: Coincident(g0,g-6)
    c: Coincident(g0,g1)
    c: Coincident(g1,g-6)
    c: Coincident(g1,g2)
    c: Coincident(g2,g-5)
    c: Coincident(g2,g3)
    c: Coincident(g3,g0)
    c: Coincident(g-8,g4)
    c: Coincident(g4,g-9)
    c: Coincident(g4,g5)
    c: Coincident(g5,g-10)
    c: Coincident(g5,g6)
    c: Coincident(g6,g-10)
    c: Coincident(g6,g7)
    c: Coincident(g7,g4)
FEATURE [Part::Extrusion] Extrude070
  Base = -> Sketch061
  Dir = (0,1,-2e-16)
  DirMode = 2
  FaceMakerClass = Part::FaceMakerBullseye
  FaceMakerMode = 3
  LengthFwd = 4.85
  LengthRev = 0
  Solid = true
  Symmetric = false
FEATURE [Part::MultiFuse] Fusion032
  Refine = true
  Shapes = -> [Extrude070,Cut036]
FEATURE [Sketcher::SketchObject] Sketch062
  ArcFitTolerance = 1e-06
  AttachmentSupport = -> [Fusion032]
  ExternalGeometry = -> [Fusion032]
  FullyConstrained = true
  MakeInternals = false
  MapMode = 5
  Placement = pos=(0,0,199.88) rot=(0,0,1;0rad)
  sketch-geometry (12):
    g0: LineSegment StartX=-9.95 StartY=-16.9003 StartZ=0 EndX=-6.1 EndY=-16.9003 EndZ=0
    g1: LineSegment StartX=-6.1 StartY=-16.9003 StartZ=0 EndX=-6.1 EndY=-17.4003 EndZ=0
    g2: LineSegment StartX=-6.1 StartY=-17.4003 StartZ=0 EndX=-6.1 EndY=-29.7803 EndZ=0
    g3: LineSegment StartX=-6.1 StartY=-29.7803 StartZ=0 EndX=-32 EndY=-29.7803 EndZ=0
    g4: LineSegment StartX=-32 StartY=-29.7803 StartZ=0 EndX=-32 EndY=-17.4003 EndZ=0
    g5: LineSegment StartX=-32 StartY=-17.4003 StartZ=0 EndX=-32 EndY=-16.9003 EndZ=0
    g6: LineSegment StartX=-32 StartY=-16.9003 StartZ=0 EndX=-28.15 EndY=-16.9003 EndZ=0
    g7: LineSegment StartX=-28.15 StartY=-16.9003 StartZ=0 EndX=-28.15 EndY=-17.4003 EndZ=0
    g8: LineSegment StartX=-28.15 StartY=-17.4003 StartZ=0 EndX=-28.15 EndY=-25.1503 EndZ=0
    g9: LineSegment StartX=-28.15 StartY=-25.1503 StartZ=0 EndX=-9.95 EndY=-25.1503 EndZ=0
    g10: LineSegment StartX=-9.95 StartY=-25.1503 StartZ=0 EndX=-9.95 EndY=-17.4003 EndZ=0
    g11: LineSegment StartX=-9.95 StartY=-17.4003 StartZ=0 EndX=-9.95 EndY=-16.9003 EndZ=0
  constraints (24):
    c: Coincident(g-13,g0)
    c: Coincident(g0,g-14)
    c: Coincident(g0,g1)
    c: Coincident(g1,g-14)
    c: Coincident(g1,g2)
    c: Coincident(g2,g-8)
    c: Coincident(g2,g3)
    c: Coincident(g3,g-6)
    c: Coincident(g3,g4)
    c: Coincident(g4,g-11)
    c: Coincident(g4,g5)
    c: Coincident(g5,g-11)
    c: Coincident(g5,g6)
    c: Coincident(g6,g-12)
    c: Coincident(g6,g7)
    c: Coincident(g7,g-12)
    c: Coincident(g7,g8)
    c: Coincident(g8,g-5)
    c: Coincident(g8,g9)
    c: Coincident(g9,g-7)
    c: Coincident(g9,g10)
    c: Coincident(g10,g-13)
    c: Coincident(g10,g11)
    c: Coincident(g11,g0)
FEATURE [Sketcher::SketchObject] Sketch063
  ArcFitTolerance = 1e-06
  AttachmentSupport = -> [Fusion032]
  ExternalGeometry = -> [Fusion032]
  FullyConstrained = true
  MakeInternals = false
  MapMode = 5
  Placement = pos=(0,2.57e-13,202.38) rot=(1,0,0;3.14159rad)
  sketch-geometry (8):
    g0: LineSegment StartX=-6.8 StartY=25.15 StartZ=0 EndX=-6.8 EndY=29.78 EndZ=0
    g1: LineSegment StartX=-10.55 StartY=25.15 StartZ=0 EndX=-10.55 EndY=29.78 EndZ=0
    g2: LineSegment StartX=-6.8 StartY=25.15 StartZ=0 EndX=-10.55 EndY=25.15 EndZ=0
    g3: LineSegment StartX=-6.8 StartY=29.78 StartZ=0 EndX=-10.55 EndY=29.78 EndZ=0
    g4: LineSegment StartX=-31.3 StartY=25.15 StartZ=0 EndX=-31.3 EndY=29.78 EndZ=0
    g5: LineSegment StartX=-27.5499 StartY=25.15 StartZ=0 EndX=-27.5499 EndY=29.78 EndZ=0
    g6: LineSegment StartX=-27.5499 StartY=25.15 StartZ=0 EndX=-31.3 EndY=25.15 EndZ=0
    g7: LineSegment StartX=-27.5499 StartY=29.78 StartZ=0 EndX=-31.3 EndY=29.78 EndZ=0
  constraints (20):
    c: Distance(g0) = 4.63
    c: Coincident(g0,g-3)
    c: Vertical(g0)
    c: Distance(g1) = 4.63
    c: Coincident(g1,g-3)
    c: Vertical(g1)
    c: Coincident(g2,g0)
    c: Coincident(g2,g1)
    c: Coincident(g3,g0)
    c: Coincident(g3,g1)
    c: Distance(g4) = 4.63
    c: Coincident(g4,g-4)
    c: Vertical(g4)
    c: Distance(g5) = 4.63
    c: Coincident(g5,g-4)
    c: Vertical(g5)
    c: Coincident(g6,g5)
    c: Coincident(g6,g4)
    c: Coincident(g7,g5)
    c: Coincident(g7,g4)
FEATURE [Part::Extrusion] Extrude071
  Base = -> Sketch063
  Dir = (0,-1.3e-15,-1)
  DirMode = 2
  FaceMakerClass = Part::FaceMakerBullseye
  FaceMakerMode = 3
  LengthFwd = 20
  LengthRev = 0
  Solid = true
  Symmetric = false
FEATURE [Part::MultiFuse] Fusion033
  Refine = true
  Shapes = -> [Fusion032,Extrude071]
FEATURE [Sketcher::SketchObject] Sketch064
  ArcFitTolerance = 1e-06
  AttachmentSupport = -> [Fusion033]
  ExternalGeometry = -> [Fusion033]
  FullyConstrained = true
  MakeInternals = false
  MapMode = 5
  Placement = pos=(-10.55,0,0) rot=(0.57735,-0.57735,-0.57735;2.0944rad)
  sketch-geometry (7):
    g0: LineSegment StartX=25.15 StartY=206.03 StartZ=0 EndX=30 EndY=206.03 EndZ=0
    g1: LineSegment StartX=30 StartY=206.03 StartZ=0 EndX=34.95 EndY=206.03 EndZ=0
    g2: LineSegment StartX=34.95 StartY=206.03 StartZ=0 EndX=34.95 EndY=202.38 EndZ=0
    g3: LineSegment StartX=34.95 StartY=202.38 StartZ=0 EndX=29.78 EndY=202.38 EndZ=0
    g4: LineSegment StartX=29.78 StartY=202.38 StartZ=0 EndX=29.78 EndY=199.88 EndZ=0
    g5: LineSegment StartX=29.78 StartY=199.88 StartZ=0 EndX=25.1503 EndY=199.88 EndZ=0
    g6: LineSegment StartX=25.1503 StartY=199.88 StartZ=0 EndX=25.15 EndY=206.03 EndZ=0
  constraints (14):
    c: Coincident(g-3,g0)
    c: Coincident(g0,g-8)
    c: Coincident(g0,g1)
    c: Coincident(g1,g-10)
    c: Coincident(g1,g2)
    c: Coincident(g2,g-11)
    c: Coincident(g2,g3)
    c: Coincident(g3,g-12)
    c: Coincident(g3,g4)
    c: Coincident(g4,g-13)
    c: Coincident(g4,g5)
    c: Coincident(g5,g-13)
    c: Coincident(g5,g6)
    c: Coincident(g6,g0)
FEATURE [Part::Extrusion] Extrude072
  Base = -> Sketch064
  Dir = (-1,0,0)
  DirMode = 2
  FaceMakerClass = Part::FaceMakerBullseye
  FaceMakerMode = 3
  LengthFwd = -0.6
  LengthRev = 0
  Solid = true
  Symmetric = false
FEATURE [Part::Cut] Cut037
  Base = -> Fusion033
  Refine = true
  Tool = -> Extrude072
FEATURE [Sketcher::SketchObject] Sketch065
  ArcFitTolerance = 1e-06
  AttachmentSupport = -> [Cut037]
  ExternalGeometry = -> [Cut037]
  FullyConstrained = true
  MakeInternals = false
  MapMode = 5
  Placement = pos=(-27.5499,0,0) rot=(0.57735,0.57735,0.57735;2.0944rad)
  sketch-geometry (6):
    g0: LineSegment StartX=-34.95 StartY=206.03 StartZ=0 EndX=-34.95 EndY=202.38 EndZ=0
    g1: LineSegment StartX=-34.95 StartY=202.38 StartZ=0 EndX=-29.78 EndY=202.38 EndZ=0
    g2: LineSegment StartX=-29.78 StartY=202.38 StartZ=0 EndX=-29.78 EndY=199.88 EndZ=0
    g3: LineSegment StartX=-29.78 StartY=199.88 StartZ=0 EndX=-25.1503 EndY=199.88 EndZ=0
    g4: LineSegment StartX=-25.1503 StartY=199.88 StartZ=0 EndX=-25.15 EndY=206.03 EndZ=0
    g5: LineSegment StartX=-25.15 StartY=206.03 StartZ=0 EndX=-34.95 EndY=206.03 EndZ=0
  constraints (12):
    c: Coincident(g-7,g0)
    c: Coincident(g0,g-7)
    c: Coincident(g0,g1)
    c: Coincident(g1,g-6)
    c: Coincident(g1,g2)
    c: Coincident(g2,g-5)
    c: Coincident(g2,g3)
    c: Coincident(g3,g-4)
    c: Coincident(g3,g4)
    c: Coincident(g4,g-3)
    c: Coincident(g4,g5)
    c: Coincident(g5,g0)
FEATURE [Part::Extrusion] Extrude073
  Base = -> Sketch065
  Dir = (1,0,0)
  DirMode = 2
  FaceMakerClass = Part::FaceMakerBullseye
  FaceMakerMode = 3
  LengthFwd = -0.6
  LengthRev = 0
  Solid = true
  Symmetric = false
FEATURE [Part::Cut] Cut038
  Base = -> Cut037
  Refine = true
  Tool = -> Extrude073
FEATURE [Sketcher::SketchObject] Sketch066
  ArcFitTolerance = 1e-06
  AttachmentSupport = -> [Cut038]
  ExternalGeometry = -> [Cut038]
  FullyConstrained = true
  MakeInternals = false
  MapMode = 5
  Placement = pos=(-6.8,0,0) rot=(0.57735,0.57735,0.57735;2.0944rad)
  sketch-geometry (6):
    g0: LineSegment StartX=-51.6 StartY=206.03 StartZ=0 EndX=-51.6 EndY=202.38 EndZ=0
    g1: LineSegment StartX=-51.6 StartY=202.38 StartZ=0 EndX=-29.78 EndY=202.38 EndZ=0
    g2: LineSegment StartX=-29.78 StartY=202.38 StartZ=0 EndX=-29.78 EndY=199.88 EndZ=0
    g3: LineSegment StartX=-25.15 StartY=206.03 StartZ=0 EndX=-25.15 EndY=199.88 EndZ=0
    g4: LineSegment StartX=-25.15 StartY=199.88 StartZ=0 EndX=-29.78 EndY=199.88 EndZ=0
    g5: LineSegment StartX=-25.15 StartY=206.03 StartZ=0 EndX=-51.6 EndY=206.03 EndZ=0
  constraints (12):
    c: Coincident(g-7,g0)
    c: Coincident(g0,g-7)
    c: Coincident(g0,g1)
    c: Coincident(g1,g-6)
    c: Coincident(g1,g2)
    c: Coincident(g2,g-6)
    c: Coincident(g-4,g3)
    c: Coincident(g3,g-4)
    c: Coincident(g3,g4)
    c: Coincident(g4,g2)
    c: Coincident(g3,g5)
    c: Coincident(g5,g0)
FEATURE [Part::Extrusion] Extrude074
  Base = -> Sketch066
  Dir = (1,0,0)
  DirMode = 2
  FaceMakerClass = Part::FaceMakerBullseye
  FaceMakerMode = 3
  LengthFwd = 0.7
  LengthRev = 0
  Solid = true
  Symmetric = false
FEATURE [Sketcher::SketchObject] Sketch067
  ArcFitTolerance = 1e-06
  AttachmentSupport = -> [Cut038]
  ExternalGeometry = -> [Cut038]
  FullyConstrained = true
  MakeInternals = false
  MapMode = 5
  Placement = pos=(-31.3,0,0) rot=(0.57735,-0.57735,-0.57735;2.0944rad)
  sketch-geometry (6):
    g0: LineSegment StartX=51.6 StartY=206.03 StartZ=0 EndX=51.6 EndY=202.38 EndZ=0
    g1: LineSegment StartX=51.6 StartY=202.38 StartZ=0 EndX=29.78 EndY=202.38 EndZ=0
    g2: LineSegment StartX=29.78 StartY=202.38 StartZ=0 EndX=29.78 EndY=199.88 EndZ=0
    g3: LineSegment StartX=29.78 StartY=199.88 StartZ=0 EndX=25.15 EndY=199.88 EndZ=0
    g4: LineSegment StartX=25.15 StartY=199.88 StartZ=0 EndX=25.15 EndY=206.03 EndZ=0
    g5: LineSegment StartX=25.15 StartY=206.03 StartZ=0 EndX=51.6 EndY=206.03 EndZ=0
  constraints (12):
    c: Coincident(g-8,g0)
    c: Coincident(g0,g-8)
    c: Coincident(g0,g1)
    c: Coincident(g1,g-6)
    c: Coincident(g1,g2)
    c: Coincident(g2,g-7)
    c: Coincident(g2,g3)
    c: Coincident(g3,g-7)
    c: Coincident(g3,g4)
    c: Coincident(g4,g-4)
    c: Coincident(g4,g5)
    c: Coincident(g5,g0)
FEATURE [Part::Extrusion] Extrude075
  Base = -> Sketch067
  Dir = (-1,0,0)
  DirMode = 2
  FaceMakerClass = Part::FaceMakerBullseye
  FaceMakerMode = 3
  LengthFwd = 0.7
  LengthRev = 0
  Solid = true
  Symmetric = false
FEATURE [Part::MultiFuse] Fusion034
  Refine = true
  Shapes = -> [Cut038,Extrude074,Extrude075]
FEATURE [Sketcher::SketchObject] Sketch068
  ArcFitTolerance = 1e-06
  AttachmentSupport = -> [Fusion034]
  ExternalGeometry = -> [Fusion034]
  FullyConstrained = true
  MakeInternals = false
  MapMode = 5
  Placement = pos=(0,-51.6003,0) rot=(0,0.707107,0.707107;3.14159rad)
  sketch-geometry (8):
    g0: LineSegment StartX=30.05 StartY=172.38 StartZ=0 EndX=30.05 EndY=183.88 EndZ=0
    g1: LineSegment StartX=32 StartY=172.38 StartZ=0 EndX=32 EndY=183.88 EndZ=0
    g2: LineSegment StartX=32 StartY=172.38 StartZ=0 EndX=30.05 EndY=172.38 EndZ=0
    g3: LineSegment StartX=32 StartY=183.88 StartZ=0 EndX=30.05 EndY=183.88 EndZ=0
    g4: LineSegment StartX=6.1 StartY=172.38 StartZ=0 EndX=6.1 EndY=183.88 EndZ=0
    g5: LineSegment StartX=8.05 StartY=172.38 StartZ=0 EndX=8.05 EndY=183.88 EndZ=0
    g6: LineSegment StartX=8.05 StartY=172.38 StartZ=0 EndX=6.1 EndY=172.38 EndZ=0
    g7: LineSegment StartX=8.05 StartY=183.88 StartZ=0 EndX=6.1 EndY=183.88 EndZ=0
  constraints (20):
    c: Distance(g0) = 11.5
    c: Coincident(g0,g-3)
    c: Vertical(g0)
    c: Distance(g1) = 11.5
    c: Coincident(g1,g-3)
    c: Vertical(g1)
    c: Coincident(g2,g1)
    c: Coincident(g2,g0)
    c: Coincident(g3,g1)
    c: Coincident(g3,g0)
    c: Distance(g4) = 11.5
    c: Coincident(g4,g-4)
    c: Vertical(g4)
    c: Distance(g5) = 11.5
    c: Coincident(g5,g-4)
    c: Vertical(g5)
    c: Coincident(g6,g5)
    c: Coincident(g6,g4)
    c: Coincident(g7,g5)
    c: Coincident(g7,g4)
FEATURE [Part::Extrusion] Extrude076
  Base = -> Sketch068
  Dir = (0,1,-2e-16)
  DirMode = 2
  FaceMakerClass = Part::FaceMakerBullseye
  FaceMakerMode = 3
  LengthFwd = 2.57
  LengthRev = 0
  Solid = true
  Symmetric = false
FEATURE [Part::MultiFuse] Fusion035  label="gun-arm"
  Refine = true
  Shapes = -> [Fusion034,Extrude076]
FEATURE [Part::Fuse] Fusion036
  Base = -> Cut011
  Tool = -> Chamfer005
FEATURE [Part::Fuse] Fusion037
  Base = -> Chamfer007
  Tool = -> Chamfer008
FEATURE [Part::Fuse] Fusion038  label="left-mag"
  Base = -> Fusion036
  Tool = -> Fusion037
FEATURE [Part::MultiFuse] Fusion039
  Shapes = -> [Chamfer006,Chamfer001]
FEATURE [Part::MultiFuse] Fusion040
  Shapes = -> [Cut013,Fusion039]
FEATURE [Part::MultiFuse] Fusion041  label="right-mag"
  Shapes = -> [Fusion040,Fusion017]
FEATURE [Mesh::Feature] Mesh004  label="left-mag-stl"
FEATURE [Mesh::Feature] Mesh005  label="right-mag-stl"
FEATURE [Part::Box] Box011  label="Cube009"
  AttacherType = Attacher::AttachEngine3D
  Height = 12
  Length = 20
  Width = 22
FEATURE [Part::Chamfer] Chamfer014
  Base = -> Box011
  EdgeLinks = -> Box011 [Edge10]
  Edges = 1 edges: [Edge10 r1=11.99 r2=21.99]
  Placement = pos=(-29.4,-51.8,172.4) rot=(0,0,1;0rad)
FEATURE [Part::Cut] Cut039  label="gun-arm-final"
  Base = -> Fusion035
  Refine = true
  Tool = -> Chamfer014
